# Revit family: CA_DWDI_CCW_DBD
name_source: partatom
category: Mechanical Equipment
units: mm (PartAtom-declared; Revit-internal decimal feet)

## family parameters
Always vertical = Yes
Cut with Voids When Loaded = No
Part Type = Normal
Room Calculation Point = No
Round Connector Dimension = Use Radius
Shared = No
Work Plane-Based = No

## types (60) — shared parameters
0 = 0' - 0"
1" = 0' - 1"
1.5 = 0' - 1 1/2"
2" = 0' - 2"
2' = 2' - 0"
3" = 0' - 3"
4" = 0' - 4"
Manufacturer = Loren Cook Company
Model = CA DWDI
ONE EIGTH = 0' - 0 1/8"
URL = www.lorencook.com

## per-type parameters (varying)
- 120_CA-DWDI_CCW_DBD_CLASS_1: ((B+.25")/2)=0' - 8 31/32"; (D-A-.25)/2=0' - 1 9/16"; (G/5*3)+2"=0' - 9 1/16"; (M-(B+.25"))/2=0' - 1 7/8"; -((B+.25")/2)=-0' - 8 31/32"; -B/2=-0' - 8 27/32"; -P=-2' - 4 11/16"; A=1' - 0 1/8"; A+.25"=1' - 0 3/8"; A+.25"+DB_H=1' - 2 3/8"; A/2=0' - 6 1/16"; B=1' - 5 11/16"; B+.25"=1' - 5 15/16"; B/2=0' - 8 27/32"; D=1' - 3 1/2"; D/2=0' - 7 3/4"; DB_D=2' - 0 3/8"; DB_E=1' - 1"; DB_F=2' - 1 3/4"; DB_G=1' - 3 1/16"; DB_H=0' - 2"; E=1' - 9 1/16"; E/2=0' - 10 17/32"; F=1' - 11 3/8"; F-((D-A)/2)=1' - 9 11/16"; F-.125"=1' - 11 1/4"; G=1' - 1"; G+((G/5*3)+2")=1' - 10 1/16"; G-(G/5*3)=0' - 4 15/16"; G-2.5"=0' - 11 9/16"; G/10*3=0' - 4 1/32"; G/5*3=0' - 8 1/16"; H=2' - 1 3/4"; INLET=1' - 4 1/8"; INLET/2=0' - 8 1/16"; J=0' - 10 11/16"; K=0' - 2"; L=0' - 10 27/32"; M=1' - 9 11/16"; M/2=0' - 10 27/32"; N=0' - 5 3/4"; P=2' - 4 11/16"; P-N=-1' - 10 15/16"; P-N-M=0' - 1 1/4"; R=0' - 1 7/16"; R+R=0' - 2 7/8"; R/2=0' - 0 23/32"; S=1' - 7 15/16"; T=0' - 9 31/32"; Type Comments=Airfoil Centrifugal Blower Counter-Clockwise Down Blast Arrangement 3 Class 1; U=0' - 7 1/2"; V=1' - 6"; W=0' - 0 11/16"; W/2=0' - 0 11/32"; X=1' - 9 15/16"; X/2=0' - 10 31/32"
- 135_CA-DWDI_CCW_DBD_CLASS_1: ((B+.25")/2)=0' - 10 3/32"; (D-A-.25)/2=0' - 1 9/16"; (G/5*3)+2"=0' - 9 13/16"; (M-(B+.25"))/2=0' - 1 7/8"; -((B+.25")/2)=-0' - 10 3/32"; -B/2=-0' - 9 31/32"; -P=-2' - 6 15/16"; A=1' - 1 5/8"; A+.25"=1' - 1 7/8"; A+.25"+DB_H=1' - 3 7/8"; A/2=0' - 6 13/16"; B=1' - 7 15/16"; B+.25"=1' - 8 3/16"; B/2=0' - 9 31/32"; D=1' - 5"; D/2=0' - 8 1/2"; DB_D=2' - 1 9/16"; DB_E=1' - 2"; DB_F=2' - 4 3/4"; DB_G=1' - 4 11/16"; DB_H=0' - 2"; E=1' - 11 5/16"; E/2=0' - 11 21/32"; F=2' - 1 5/8"; F-((D-A)/2)=1' - 11 15/16"; F-.125"=2' - 1 1/2"; G=1' - 2"; G+((G/5*3)+2")=1' - 11 13/16"; G-(G/5*3)=0' - 5 3/16"; G-2.5"=1' - 0 9/16"; G/10*3=0' - 4 13/32"; G/5*3=0' - 8 13/16"; H=2' - 4 3/4"; INLET=1' - 5 5/8"; INLET/2=0' - 8 13/16"; J=1' - 0 1/16"; K=0' - 2"; L=0' - 11 31/32"; M=1' - 11 15/16"; M/2=0' - 11 31/32"; N=0' - 5 3/4"; P=2' - 6 15/16"; P-N=-2' - 1 3/16"; P-N-M=0' - 1 1/4"; R=0' - 1 7/16"; R+R=0' - 2 7/8"; R/2=0' - 0 23/32"; S=1' - 10 3/16"; T=0' - 11 3/32"; Type Comments=Airfoil Centrifugal Blower Counter-Clockwise Down Blast Arrangement 3 Class 1; U=0' - 8 1/2"; V=1' - 6"; W=0' - 0 11/16"; W/2=0' - 0 11/32"; X=2' - 0 3/16"; X/2=1' - 0 3/32"
- 150_CA-DWDI_CCW_DBD_CLASS_1: ((B+.25")/2)=0' - 11 1/8"; (D-A-.25)/2=0' - 1 9/16"; (G/5*3)+2"=0' - 10 9/16"; (M-(B+.25"))/2=0' - 1 7/8"; -((B+.25")/2)=-0' - 11 1/8"; -B/2=-0' - 11"; -P=-2' - 10 1/4"; A=1' - 3 1/4"; A+.25"=1' - 3 1/2"; A+.25"+DB_H=1' - 5 1/2"; A/2=0' - 7 5/8"; B=1' - 10"; B+.25"=1' - 10 1/4"; B/2=0' - 11"; D=1' - 6 5/8"; D/2=0' - 9 5/16"; DB_D=2' - 5 1/4"; DB_E=1' - 3"; DB_F=2' - 7 5/8"; DB_G=1' - 6 5/16"; DB_H=0' - 2"; E=2' - 1 3/8"; E/2=1' - 0 11/16"; F=2' - 3 15/16"; F-((D-A)/2)=2' - 2 1/4"; F-.125"=2' - 3 13/16"; G=1' - 3"; G+((G/5*3)+2")=2' - 1 9/16"; G-(G/5*3)=0' - 5 7/16"; G-2.5"=1' - 1 5/16"; G/10*3=0' - 4 25/32"; G/5*3=0' - 9 9/16"; H=2' - 7 5/8"; INLET=1' - 7 1/8"; INLET/2=0' - 9 9/16"; J=1' - 1 5/16"; K=0' - 2"; L=1' - 1"; M=2' - 2"; M/2=1' - 1"; N=0' - 6 5/8"; P=2' - 10 1/4"; P-N=-2' - 3 5/8"; P-N-M=0' - 1 5/8"; R=0' - 1 11/16"; R+R=0' - 3 3/8"; R/2=0' - 0 27/32"; S=2' - 0 1/4"; T=1' - 0 1/8"; Type Comments=Airfoil Centrifugal Blower Counter-Clockwise Down Blast Arrangement 3 Class 1; U=0' - 9"; V=1' - 6"; W=0' - 0 11/16"; W/2=0' - 0 11/32"; X=2' - 2 1/4"; X/2=1' - 1 1/8"
- 165_CA-DWDI_CCW_DBD_CLASS_1: ((B+.25")/2)=1' - 0 1/8"; (D-A-.25)/2=0' - 1 9/16"; (G/5*3)+2"=0' - 11 19/32"; (M-(B+.25"))/2=0' - 1 7/8"; -((B+.25")/2)=-1' - 0 1/8"; -B/2=-1' - 0"; -P=-3' - 0 1/4"; A=1' - 4 15/16"; A+.25"=1' - 5 3/16"; A+.25"+DB_H=1' - 7 3/16"; A/2=0' - 8 15/32"; B=2' - 0"; B+.25"=2' - 0 1/4"; B/2=1' - 0"; D=1' - 8 5/16"; D/2=0' - 10 5/32"; DB_D=2' - 8 5/8"; DB_E=1' - 5"; DB_F=2' - 10 3/8"; DB_G=1' - 7 15/16"; DB_H=0' - 2"; E=2' - 3 3/8"; E/2=1' - 1 11/16"; F=2' - 7 1/4"; F-((D-A)/2)=2' - 5 9/16"; F-.125"=2' - 7 1/8"; G=1' - 5"; G+((G/5*3)+2")=2' - 4 19/32"; G-(G/5*3)=0' - 6 13/32"; G-2.5"=1' - 3 5/16"; G/10*3=0' - 5 5/16"; G/5*3=0' - 10 19/32"; H=2' - 10 3/8"; INLET=1' - 9 3/16"; INLET/2=0' - 10 19/32"; J=1' - 2 7/16"; K=0' - 2"; L=1' - 2"; M=2' - 4"; M/2=1' - 2"; N=0' - 6 5/8"; P=3' - 0 1/4"; P-N=-2' - 5 5/8"; P-N-M=0' - 1 5/8"; R=0' - 1 11/16"; R+R=0' - 3 3/8"; R/2=0' - 0 27/32"; S=2' - 2 1/4"; T=1' - 1 1/8"; Type Comments=Airfoil Centrifugal Blower Counter-Clockwise Down Blast Arrangement 3 Class 1; U=0' - 10"; V=1' - 6"; W=0' - 0 11/16"; W/2=0' - 0 11/32"; X=2' - 4 1/4"; X/2=1' - 2 1/8"
- 180_CA-DWDI_CCW_DBD_CLASS_1: ((B+.25")/2)=1' - 1 5/32"; (D-A-.25)/2=0' - 1 9/16"; (G/5*3)+2"=1' - 0 11/32"; (M-(B+.25"))/2=0' - 1 7/8"; -((B+.25")/2)=-1' - 1 5/32"; -B/2=-1' - 1 1/32"; -P=-3' - 2 13/16"; A=1' - 6 1/2"; A+.25"=1' - 6 3/4"; A+.25"+DB_H=1' - 8 3/4"; A/2=0' - 9 1/4"; B=2' - 2 1/16"; B+.25"=2' - 2 5/16"; B/2=1' - 1 1/32"; D=1' - 9 7/8"; D/2=0' - 10 15/16"; DB_D=2' - 11 1/8"; DB_E=1' - 6"; DB_F=3' - 1 1/8"; DB_G=1' - 9 9/16"; DB_H=0' - 2"; E=2' - 5 7/16"; E/2=1' - 2 23/32"; F=2' - 9 1/2"; F-((D-A)/2)=2' - 7 13/16"; F-.125"=2' - 9 3/8"; G=1' - 6"; G+((G/5*3)+2")=2' - 6 11/32"; G-(G/5*3)=0' - 6 21/32"; G-2.5"=1' - 4 5/16"; G/10*3=0' - 5 11/16"; G/5*3=0' - 11 11/32"; H=3' - 1 1/8"; INLET=1' - 10 11/16"; INLET/2=0' - 11 11/32"; J=1' - 3 9/16"; K=0' - 2"; L=1' - 3 1/32"; M=2' - 6 1/16"; M/2=1' - 3 1/32"; N=0' - 7 1/8"; P=3' - 2 13/16"; P-N=-2' - 7 11/16"; P-N-M=0' - 1 5/8"; R=0' - 1 11/16"; R+R=0' - 3 3/8"; R/2=0' - 0 27/32"; S=2' - 4 5/16"; T=1' - 2 5/32"; Type Comments=Airfoil Centrifugal Blower Counter-Clockwise Down Blast Arrangement 3 Class 1; U=0' - 11"; V=1' - 6"; W=0' - 0 11/16"; W/2=0' - 0 11/32"; X=2' - 6 5/16"; X/2=1' - 3 5/32"
- 195_CA-DWDI_CCW_DBD_CLASS_1: ((B+.25")/2)=1' - 2 11/32"; (D-A-.25)/2=0' - 1 9/16"; (G/5*3)+2"=1' - 1 3/32"; (M-(B+.25"))/2=0' - 1 7/8"; -((B+.25")/2)=-1' - 2 11/32"; -B/2=-1' - 2 7/32"; -P=-3' - 5 11/16"; A=1' - 7 1/2"; A+.25"=1' - 7 3/4"; A+.25"+DB_H=1' - 9 3/4"; A/2=0' - 9 3/4"; B=2' - 4 7/16"; B+.25"=2' - 4 11/16"; B/2=1' - 2 7/32"; D=1' - 10 7/8"; D/2=0' - 11 7/16"; DB_D=3' - 2 1/2"; DB_E=1' - 8"; DB_F=3' - 4"; DB_G=1' - 11 3/16"; DB_H=0' - 2"; E=2' - 7 13/16"; E/2=1' - 3 29/32"; F=3' - 0 13/16"; F-((D-A)/2)=2' - 11 1/8"; F-.125"=3' - 0 11/16"; G=1' - 8"; G+((G/5*3)+2")=2' - 9 3/32"; G-(G/5*3)=0' - 7 29/32"; G-2.5"=1' - 6 1/16"; G/10*3=0' - 6 1/16"; G/5*3=1' - 0 3/32"; H=3' - 4"; INLET=2' - 0 3/16"; INLET/2=1' - 0 3/32"; J=1' - 4 13/16"; K=0' - 2"; L=1' - 4 7/32"; M=2' - 8 7/16"; M/2=1' - 4 7/32"; N=0' - 7 1/4"; P=3' - 5 11/16"; P-N=-2' - 10 7/16"; P-N-M=0' - 2"; R=0' - 1 15/16"; R+R=0' - 3 7/8"; R/2=0' - 0 31/32"; S=2' - 6 11/16"; T=1' - 3 11/32"; Type Comments=Airfoil Centrifugal Blower Counter-Clockwise Down Blast Arrangement 3 Class 1; U=0' - 11 1/2"; V=0' - 6"; W=0' - 0 11/16"; W/2=0' - 0 11/32"; X=2' - 8 11/16"; X/2=1' - 4 11/32"
- 210_CA-DWDI_CCW_DBD_CLASS_1: ((B+.25")/2)=1' - 3 5/16"; (D-A-.25)/2=0' - 1 9/16"; (G/5*3)+2"=1' - 1 31/32"; (M-(B+.25"))/2=0' - 1 7/8"; -((B+.25")/2)=-1' - 3 5/16"; -B/2=-1' - 3 3/16"; -P=-3' - 8 1/8"; A=1' - 9 5/8"; A+.25"=1' - 9 7/8"; A+.25"+DB_H=1' - 11 7/8"; A/2=0' - 10 13/16"; B=2' - 6 3/8"; B+.25"=2' - 6 5/8"; B/2=1' - 3 3/16"; D=2' - 1"; D/2=1' - 0 1/2"; DB_D=3' - 4 15/16"; DB_E=1' - 9"; DB_F=3' - 6 7/8"; DB_G=2' - 0 7/8"; DB_H=0' - 2"; E=2' - 9 3/4"; E/2=1' - 4 7/8"; F=3' - 3 1/8"; F-((D-A)/2)=3' - 1 7/16"; F-.125"=3' - 3"; G=1' - 9"; G+((G/5*3)+2")=2' - 10 31/32"; G-(G/5*3)=0' - 8 1/32"; G-2.5"=1' - 7 1/16"; G/10*3=0' - 6 1/2"; G/5*3=1' - 0 31/32"; H=3' - 6 7/8"; INLET=2' - 1 15/16"; INLET/2=1' - 0 31/32"; J=1' - 6"; K=0' - 2"; L=1' - 5 3/16"; M=2' - 10 3/8"; M/2=1' - 5 3/16"; N=0' - 7 7/8"; P=3' - 8 1/8"; P-N=-3' - 0 1/4"; P-N-M=0' - 1 7/8"; R=0' - 1 15/16"; R+R=0' - 3 7/8"; R/2=0' - 0 31/32"; S=2' - 8 5/8"; T=1' - 4 5/16"; Type Comments=Airfoil Centrifugal Blower Counter-Clockwise Down Blast Arrangement 3 Class 1; U=1' - 0"; V=0' - 7"; W=0' - 0 13/16"; W/2=0' - 0 13/32"; X=2' - 10 5/8"; X/2=1' - 5 5/16"
- 225_CA-DWDI_CCW_DBD_CLASS_1: ((B+.25")/2)=1' - 4 3/8"; (D-A-.25)/2=0' - 1 9/16"; (G/5*3)+2"=1' - 2 23/32"; (M-(B+.25"))/2=0' - 1 7/8"; -((B+.25")/2)=-1' - 4 3/8"; -B/2=-1' - 4 1/4"; -P=-4' - 0 1/4"; A=1' - 11 3/16"; A+.25"=1' - 11 7/16"; A+.25"+DB_H=2' - 1 7/16"; A/2=0' - 11 19/32"; B=2' - 8 1/2"; B+.25"=2' - 8 3/4"; B/2=1' - 4 1/4"; D=2' - 2 9/16"; D/2=1' - 1 9/32"; DB_D=3' - 8 3/8"; DB_E=1' - 11"; DB_F=3' - 9 3/4"; DB_G=2' - 2 1/2"; DB_H=0' - 2"; E=2' - 11 7/8"; E/2=1' - 5 15/16"; F=3' - 6 3/8"; F-((D-A)/2)=3' - 4 11/16"; F-.125"=3' - 6 1/4"; G=1' - 11"; G+((G/5*3)+2")=3' - 1 23/32"; G-(G/5*3)=0' - 9 9/32"; G-2.5"=1' - 9 1/16"; G/10*3=0' - 6 7/8"; G/5*3=1' - 1 23/32"; H=3' - 9 3/4"; INLET=2' - 3 7/16"; INLET/2=1' - 1 23/32"; J=1' - 7 1/4"; K=0' - 2"; L=1' - 6 1/4"; M=3' - 0 1/2"; M/2=1' - 6 1/4"; N=0' - 7 7/8"; P=4' - 0 1/4"; P-N=-3' - 4 3/8"; P-N-M=0' - 3 7/8"; R=0' - 1 15/16"; R+R=0' - 3 7/8"; R/2=0' - 0 31/32"; S=2' - 10 3/4"; T=1' - 5 3/8"; Type Comments=Airfoil Centrifugal Blower Counter-Clockwise Down Blast Arrangement 3 Class 1; U=1' - 0 1/2"; V=0' - 7 1/2"; W=0' - 0 13/16"; W/2=0' - 0 13/32"; X=3' - 0 3/4"; X/2=1' - 6 3/8"
- 245_CA-DWDI_CCW_DBD_CLASS_1: ((B+.25")/2)=1' - 5 21/32"; (D-A-.25)/2=0' - 1 9/16"; (G/5*3)+2"=1' - 3 23/32"; (M-(B+.25"))/2=0' - 1 7/8"; -((B+.25")/2)=-1' - 5 21/32"; -B/2=-1' - 5 17/32"; -P=-4' - 1 13/16"; A=2' - 1 1/2"; A+.25"=2' - 1 3/4"; A+.25"+DB_H=2' - 3 3/4"; A/2=1' - 0 3/4"; B=2' - 11 1/16"; B+.25"=2' - 11 5/16"; B/2=1' - 5 17/32"; D=2' - 4 7/8"; D/2=1' - 2 7/16"; DB_D=4' - 0 1/4"; DB_E=2' - 1"; DB_F=4' - 1 1/2"; DB_G=2' - 4 5/8"; DB_H=0' - 2"; E=3' - 2 7/16"; E/2=1' - 7 7/32"; F=3' - 10 1/8"; F-((D-A)/2)=3' - 8 7/16"; F-.125"=3' - 10"; G=2' - 1"; G+((G/5*3)+2")=3' - 4 23/32"; G-(G/5*3)=0' - 10 9/32"; G-2.5"=1' - 10 13/16"; G/10*3=0' - 7 3/8"; G/5*3=1' - 2 23/32"; H=4' - 1 1/2"; INLET=2' - 5 7/16"; INLET/2=1' - 2 23/32"; J=1' - 8 7/8"; K=0' - 2"; L=1' - 7 17/32"; M=3' - 3 1/16"; M/2=1' - 7 17/32"; N=0' - 8 5/8"; P=4' - 1 13/16"; P-N=-3' - 5 3/16"; P-N-M=0' - 2 1/8"; R=0' - 2 3/16"; R+R=0' - 4 3/8"; R/2=0' - 1 3/32"; S=3' - 1 5/16"; T=1' - 6 21/32"; Type Comments=Airfoil Centrifugal Blower Counter-Clockwise Down Blast Arrangement 3 Class 1; U=1' - 1 1/2"; V=0' - 8"; W=0' - 0 13/16"; W/2=0' - 0 13/32"; X=3' - 5 5/16"; X/2=1' - 8 21/32"
- 270_CA-DWDI_CCW_DBD_CLASS_1: ((B+.25")/2)=1' - 7 27/32"; (D-A-.25)/2=0' - 1 9/16"; (G/5*3)+2"=1' - 4 31/32"; (M-(B+.25"))/2=0' - 1 7/8"; -((B+.25")/2)=-1' - 7 27/32"; -B/2=-1' - 7 23/32"; -P=-4' - 6 3/16"; A=2' - 3 1/2"; A+.25"=2' - 3 3/4"; A+.25"+DB_H=2' - 5 3/4"; A/2=1' - 1 3/4"; B=3' - 3 7/16"; B+.25"=3' - 3 11/16"; B/2=1' - 7 23/32"; D=2' - 6 7/8"; D/2=1' - 3 7/16"; DB_D=4' - 2 1/8"; DB_E=2' - 3"; DB_F=4' - 6 3/4"; DB_G=2' - 7 3/8"; DB_H=0' - 2"; E=3' - 6 13/16"; E/2=1' - 9 13/32"; F=4' - 2 1/4"; F-((D-A)/2)=4' - 0 9/16"; F-.125"=4' - 2 1/8"; G=2' - 3"; G+((G/5*3)+2")=3' - 7 31/32"; G-(G/5*3)=0' - 11 1/32"; G-2.5"=2' - 0 13/16"; G/10*3=0' - 8"; G/5*3=1' - 3 31/32"; H=4' - 6 3/4"; INLET=2' - 7 15/16"; INLET/2=1' - 3 31/32"; J=1' - 11 3/8"; K=0' - 2"; L=1' - 9 23/32"; M=3' - 7 7/16"; M/2=1' - 9 23/32"; N=0' - 8 5/8"; P=4' - 6 3/16"; P-N=-3' - 9 9/16"; P-N-M=0' - 2 1/8"; R=0' - 2 3/16"; R+R=0' - 4 3/8"; R/2=0' - 1 3/32"; S=3' - 5 11/16"; T=1' - 8 27/32"; Type Comments=Airfoil Centrifugal Blower Counter-Clockwise Down Blast Arrangement 3 Class 1; U=1' - 3"; V=0' - 9"; W=0' - 0 13/16"; W/2=0' - 0 13/32"; X=3' - 9 11/16"; X/2=1' - 10 27/32"
- 300_CA-DWDI_CCW_DBD_CLASS_1: ((B+.25")/2)=1' - 9 5/8"; (D-A-.25)/2=0' - 1 19/32"; (G/5*3)+2"=1' - 6 15/32"; (M-(B+.25"))/2=0' - 1 7/8"; -((B+.25")/2)=-1' - 9 5/8"; -B/2=-1' - 9 1/2"; -P=-4' - 10 1/2"; A=2' - 7 3/16"; A+.25"=2' - 7 7/16"; A+.25"+DB_H=2' - 9 7/16"; A/2=1' - 3 19/32"; B=3' - 7"; B+.25"=3' - 7 1/4"; B/2=1' - 9 1/2"; D=2' - 10 5/8"; D/2=1' - 5 5/16"; DB_D=4' - 10 1/2"; DB_E=2' - 6"; DB_F=5' - 0"; DB_G=2' - 10 5/8"; DB_H=0' - 2"; E=3' - 10 7/16"; E/2=1' - 11 7/32"; F=4' - 7 7/8"; F-((D-A)/2)=4' - 6 5/32"; F-.125"=4' - 7 3/4"; G=2' - 6"; G+((G/5*3)+2")=4' - 0 15/32"; G-(G/5*3)=1' - 0 17/32"; G-2.5"=2' - 3 9/16"; G/10*3=0' - 8 3/4"; G/5*3=1' - 5 15/32"; H=5' - 0"; INLET=2' - 10 15/16"; INLET/2=1' - 5 15/32"; J=2' - 1 3/8"; K=0' - 2"; L=1' - 11 1/2"; M=3' - 11"; M/2=1' - 11 1/2"; N=0' - 9 1/4"; P=4' - 10 1/2"; P-N=-4' - 1 1/4"; P-N-M=0' - 2 1/4"; R=0' - 2 7/16"; R+R=0' - 4 7/8"; R/2=0' - 1 7/32"; S=3' - 9 1/4"; T=1' - 10 5/8"; Type Comments=Airfoil Centrifugal Blower Counter-Clockwise Down Blast Arrangement 3 Class 1; U=1' - 4 1/2"; V=0' - 10"; W=0' - 0 13/16"; W/2=0' - 0 13/32"; X=4' - 1 1/4"; X/2=2' - 0 5/8"
- 330_CA-DWDI_CCW_DBD_CLASS_1: ((B+.25")/2)=1' - 11 21/32"; (D-A-.25)/2=0' - 2 3/32"; (G/5*3)+2"=1' - 7 31/32"; (M-(B+.25"))/2=0' - 1 7/8"; -((B+.25")/2)=-1' - 11 21/32"; -B/2=-1' - 11 17/32"; -P=-5' - 3 9/16"; A=2' - 10 1/2"; A+.25"=2' - 10 3/4"; A+.25"+DB_H=3' - 0 3/4"; A/2=1' - 5 1/4"; B=3' - 11 1/16"; B+.25"=3' - 11 5/16"; B/2=1' - 11 17/32"; D=3' - 2 15/16"; D/2=1' - 7 15/32"; DB_D=5' - 4 3/8"; DB_E=2' - 9"; DB_F=5' - 5 3/4"; DB_G=3' - 1 7/8"; DB_H=0' - 2"; E=4' - 3 1/2"; E/2=2' - 1 3/4"; F=5' - 1 3/8"; F-((D-A)/2)=4' - 11 5/32"; F-.125"=5' - 1 1/4"; G=2' - 9"; G+((G/5*3)+2")=4' - 4 31/32"; G-(G/5*3)=1' - 2 1/32"; G-2.5"=2' - 6 5/16"; G/10*3=0' - 9 1/2"; G/5*3=1' - 6 31/32"; H=5' - 5 3/4"; INLET=3' - 1 15/16"; INLET/2=1' - 6 31/32"; J=2' - 3 7/8"; K=0' - 2"; L=2' - 1 17/32"; M=4' - 3 1/16"; M/2=2' - 1 17/32"; N=0' - 10 1/16"; P=5' - 3 9/16"; P-N=-4' - 5 1/2"; P-N-M=0' - 2 7/16"; R=0' - 2 11/16"; R+R=0' - 5 3/8"; R/2=0' - 1 11/32"; S=4' - 1 5/16"; T=2' - 0 21/32"; Type Comments=Airfoil Centrifugal Blower Counter-Clockwise Down Blast Arrangement 3 Class 1; U=1' - 6"; V=1' - 0"; W=0' - 0 13/16"; W/2=0' - 0 13/32"; X=4' - 5 7/16"; X/2=2' - 2 23/32"
- 365_CA-DWDI_CCW_DBD_CLASS_1: ((B+.25")/2)=2' - 2 7/32"; (D-A-.25)/2=0' - 2 3/32"; (G/5*3)+2"=1' - 9 23/32"; (M-(B+.25"))/2=0' - 1 7/8"; -((B+.25")/2)=-2' - 2 7/32"; -B/2=-2' - 2 3/32"; -P=-5' - 9 5/16"; A=3' - 2 11/16"; A+.25"=3' - 2 15/16"; A+.25"+DB_H=3' - 4 15/16"; A/2=1' - 7 11/32"; B=4' - 4 3/16"; B+.25"=4' - 4 7/16"; B/2=2' - 2 3/32"; D=3' - 7 1/8"; D/2=1' - 9 9/16"; DB_D=5' - 10 5/8"; DB_E=3' - 0"; DB_F=6' - 0 3/8"; DB_G=3' - 5 3/4"; DB_H=0' - 2"; E=4' - 8 5/8"; E/2=2' - 4 5/16"; F=5' - 7 7/16"; F-((D-A)/2)=5' - 5 7/32"; F-.125"=5' - 7 5/16"; G=3' - 0"; G+((G/5*3)+2")=4' - 9 23/32"; G-(G/5*3)=1' - 3 9/32"; G-2.5"=2' - 9 13/16"; G/10*3=0' - 10 3/8"; G/5*3=1' - 8 23/32"; H=6' - 0 3/8"; INLET=3' - 5 7/16"; INLET/2=1' - 8 23/32"; J=2' - 6 5/8"; K=0' - 2"; L=2' - 4 3/32"; M=4' - 8 3/16"; M/2=2' - 4 3/32"; N=0' - 10 5/16"; P=5' - 9 5/16"; P-N=-4' - 11"; P-N-M=0' - 2 13/16"; R=0' - 2 3/16"; R+R=0' - 4 3/8"; R/2=0' - 1 3/32"; S=4' - 6 7/16"; T=2' - 3 7/32"; Type Comments=Airfoil Centrifugal Blower Counter-Clockwise Down Blast Arrangement 3 Class 1; U=1' - 8"; V=1' - 1"; W=0' - 0 13/16"; W/2=0' - 0 13/32"; X=4' - 10 9/16"; X/2=2' - 5 9/32"
- 402_CA-DWDI_CCW_DBD_CLASS_1: ((B+.25")/2)=2' - 5 1/32"; (D-A-.25)/2=0' - 2 3/32"; (G/5*3)+2"=1' - 11 19/32"; (M-(B+.25"))/2=0' - 2 7/8"; -((B+.25")/2)=-2' - 5 1/32"; -B/2=-2' - 4 29/32"; -P=-6' - 3 11/16"; A=3' - 5 3/4"; A+.25"=3' - 6"; A+.25"+DB_H=3' - 9"; A/2=1' - 8 7/8"; B=4' - 9 13/16"; B+.25"=4' - 10 1/16"; B/2=2' - 4 29/32"; D=3' - 10 3/16"; D/2=1' - 11 3/32"; DB_D=6' - 6 1/4"; DB_E=3' - 4"; DB_F=6' - 8 3/8"; DB_G=3' - 10 3/4"; DB_H=0' - 3"; E=5' - 2 1/4"; E/2=2' - 7 1/8"; F=6' - 2 11/16"; F-((D-A)/2)=6' - 0 15/32"; F-.125"=6' - 2 9/16"; G=3' - 4"; G+((G/5*3)+2")=5' - 3 19/32"; G-(G/5*3)=1' - 5 13/32"; G-2.5"=3' - 1 9/16"; G/10*3=0' - 11 5/16"; G/5*3=1' - 10 19/32"; H=6' - 8 3/8"; INLET=3' - 9 3/16"; INLET/2=1' - 10 19/32"; J=2' - 9 5/8"; K=0' - 3"; L=2' - 7 29/32"; M=5' - 3 13/16"; M/2=2' - 7 29/32"; N=0' - 10"; P=6' - 3 11/16"; P-N=-5' - 5 11/16"; P-N-M=0' - 1 7/8"; R=0' - 2 7/16"; R+R=0' - 4 7/8"; R/2=0' - 1 7/32"; S=5' - 1 5/16"; T=2' - 6 21/32"; Type Comments=Airfoil Centrifugal Blower Counter-Clockwise Down Blast Arrangement 3 Class 1; U=1' - 10"; V=1' - 2"; W=0' - 1 1/16"; W/2=0' - 0 17/32"; X=5' - 5 3/16"; X/2=2' - 8 19/32"
- 445_CA-DWDI_CCW_DBD_CLASS_1: ((B+.25")/2)=2' - 8 1/4"; (D-A-.25)/2=0' - 2 3/32"; (G/5*3)+2"=2' - 1 23/32"; (M-(B+.25"))/2=0' - 2 7/8"; -((B+.25")/2)=-2' - 8 1/4"; -B/2=-2' - 8 1/8"; -P=-6' - 10 5/8"; A=3' - 9 15/16"; A+.25"=3' - 10 3/16"; A+.25"+DB_H=4' - 1 3/16"; A/2=1' - 10 31/32"; B=5' - 4 1/4"; B+.25"=5' - 4 1/2"; B/2=2' - 8 1/8"; D=4' - 2 3/8"; D/2=2' - 1 3/16"; DB_D=7' - 2 1/4"; DB_E=3' - 8"; DB_F=7' - 4 1/2"; DB_G=4' - 3 3/8"; DB_H=0' - 3"; E=5' - 8 11/16"; E/2=2' - 10 11/32"; F=6' - 10 5/16"; F-((D-A)/2)=6' - 8 3/32"; F-.125"=6' - 10 3/16"; G=3' - 8"; G+((G/5*3)+2")=5' - 9 23/32"; G-(G/5*3)=1' - 7 9/32"; G-2.5"=3' - 5 9/16"; G/10*3=1' - 0 3/8"; G/5*3=2' - 0 23/32"; H=7' - 4 1/2"; INLET=4' - 1 7/16"; INLET/2=2' - 0 23/32"; J=3' - 1 1/8"; K=0' - 3"; L=2' - 11 1/8"; M=5' - 10 1/4"; M/2=2' - 11 1/8"; N=0' - 10 5/8"; P=6' - 10 5/8"; P-N=-6' - 0"; P-N-M=0' - 1 3/4"; R=0' - 2 7/16"; R+R=0' - 4 7/8"; R/2=0' - 1 7/32"; S=5' - 7 3/4"; T=2' - 9 7/8"; Type Comments=Airfoil Centrifugal Blower Counter-Clockwise Down Blast Arrangement 3 Class 1; U=2' - 0"; V=1' - 4"; W=0' - 1 1/16"; W/2=0' - 0 17/32"; X=5' - 11 5/8"; X/2=2' - 11 13/16"
- 490_CA-DWDI_CCW_DBD_CLASS_1: ((B+.25")/2)=2' - 11 3/16"; (D-A-.25)/2=0' - 2 3/32"; (G/5*3)+2"=2' - 4 1/2"; (M-(B+.25"))/2=0' - 2 7/8"; -((B+.25")/2)=-2' - 11 3/16"; -B/2=-2' - 11 1/16"; -P=-7' - 5 1/2"; A=4' - 3"; A+.25"=4' - 3 1/4"; A+.25"+DB_H=4' - 6 1/4"; A/2=2' - 1 1/2"; B=5' - 10 1/8"; B+.25"=5' - 10 3/8"; B/2=2' - 11 1/16"; D=4' - 7 7/16"; D/2=2' - 3 23/32"; DB_D=7' - 10 1/2"; DB_E=4' - 0"; DB_F=8' - 1"; DB_G=4' - 8 1/4"; DB_H=0' - 3"; E=6' - 2 9/16"; E/2=3' - 1 9/32"; F=7' - 6 3/16"; F-((D-A)/2)=7' - 3 31/32"; F-.125"=7' - 6 1/16"; G=4' - 0"; G+((G/5*3)+2")=6' - 4 1/2"; G-(G/5*3)=1' - 8 1/2"; G-2.5"=3' - 9 1/16"; G/10*3=1' - 1 3/4"; G/5*3=2' - 3 1/2"; H=8' - 1"; INLET=4' - 7"; INLET/2=2' - 3 1/2"; J=3' - 4 3/4"; K=0' - 3"; L=3' - 2 1/16"; M=6' - 4 1/8"; M/2=3' - 2 1/16"; N=0' - 11 1/2"; P=7' - 5 1/2"; P-N=-6' - 6"; P-N-M=0' - 1 7/8"; R=0' - 2 15/16"; R+R=0' - 5 7/8"; R/2=0' - 1 15/32"; S=6' - 1 5/8"; T=3' - 0 13/16"; Type Comments=Airfoil Centrifugal Blower Counter-Clockwise Down Blast Arrangement 3 Class 1; U=2' - 2 1/2"; V=1' - 6"; W=0' - 1 1/16"; W/2=0' - 0 17/32"; X=6' - 5 1/2"; X/2=3' - 2 3/4"
- 540_CA-DWDI_CCW_DBD_CLASS_1: ((B+.25")/2)=3' - 3 3/32"; (D-A-.25)/2=0' - 2 3/32"; (G/5*3)+2"=2' - 7"; (M-(B+.25"))/2=0' - 2 7/8"; -((B+.25")/2)=-3' - 3 3/32"; -B/2=-3' - 2 31/32"; -P=-8' - 2 5/16"; A=4' - 7 3/4"; A+.25"=4' - 8"; A+.25"+DB_H=4' - 11"; A/2=2' - 3 7/8"; B=6' - 5 15/16"; B+.25"=6' - 6 3/16"; B/2=3' - 2 31/32"; D=5' - 0 3/16"; D/2=2' - 6 3/32"; DB_D=8' - 8 1/4"; DB_E=4' - 5"; DB_F=8' - 10 5/8"; DB_G=5' - 1 3/4"; DB_H=0' - 3"; E=6' - 10 3/8"; E/2=3' - 5 3/16"; F=8' - 3 1/2"; F-((D-A)/2)=8' - 1 9/32"; F-.125"=8' - 3 3/8"; G=4' - 5"; G+((G/5*3)+2")=7' - 0"; G-(G/5*3)=1' - 11"; G-2.5"=4' - 1 9/16"; G/10*3=1' - 3"; G/5*3=2' - 6"; H=8' - 10 5/8"; INLET=5' - 0"; INLET/2=2' - 6"; J=3' - 8 7/8"; K=0' - 3"; L=3' - 5 31/32"; M=6' - 11 15/16"; M/2=3' - 5 31/32"; N=1' - 0 7/16"; P=8' - 2 5/16"; P-N=-7' - 1 7/8"; P-N-M=0' - 1 15/16"; R=0' - 3 7/16"; R+R=0' - 6 7/8"; R/2=0' - 1 23/32"; S=6' - 9 7/16"; T=3' - 4 23/32"; Type Comments=Airfoil Centrifugal Blower Counter-Clockwise Down Blast Arrangement 3 Class 1; U=2' - 5"; V=1' - 8"; W=0' - 1 1/16"; W/2=0' - 0 17/32"; X=7' - 4 5/16"; X/2=3' - 8 5/32"
- 600_CA-DWDI_CCW_DBD_CLASS_1: ((B+.25")/2)=3' - 7 1/4"; (D-A-.25)/2=0' - 2 3/32"; (G/5*3)+2"=2' - 10"; (M-(B+.25"))/2=0' - 2 7/8"; -((B+.25")/2)=-3' - 7 1/4"; -B/2=-3' - 7 1/8"; -P=-8' - 11 1/2"; A=5' - 2 3/16"; A+.25"=5' - 2 7/16"; A+.25"+DB_H=5' - 5 7/16"; A/2=2' - 7 3/32"; B=7' - 2 1/4"; B+.25"=7' - 2 1/2"; B/2=3' - 7 1/8"; D=5' - 6 5/8"; D/2=2' - 9 5/16"; DB_D=9' - 8"; DB_E=4' - 11"; DB_F=9' - 10"; DB_G=5' - 8 1/4"; DB_H=0' - 3"; E=7' - 6 11/16"; E/2=3' - 9 11/32"; F=9' - 2 11/16"; F-((D-A)/2)=9' - 0 15/32"; F-.125"=9' - 2 9/16"; G=4' - 11"; G+((G/5*3)+2")=7' - 9"; G-(G/5*3)=2' - 2"; G-2.5"=4' - 7 9/16"; G/10*3=1' - 4 1/2"; G/5*3=2' - 9"; H=9' - 10"; INLET=5' - 6"; INLET/2=2' - 9"; J=4' - 1 3/4"; K=0' - 3"; L=3' - 10 1/8"; M=7' - 8 1/4"; M/2=3' - 10 1/8"; N=1' - 1"; P=8' - 11 1/2"; P-N=-7' - 10 1/2"; P-N-M=0' - 2 1/4"; R=0' - 3 7/16"; R+R=0' - 6 7/8"; R/2=0' - 1 23/32"; S=7' - 5 3/4"; T=3' - 8 7/8"; Type Comments=Airfoil Centrifugal Blower Counter-Clockwise Down Blast Arrangement 3 Class 1; U=2' - 8"; V=1' - 10"; W=0' - 1 1/16"; W/2=0' - 0 17/32"; X=8' - 0 5/8"; X/2=4' - 0 5/16"
- 660_CA-DWDI_CCW_DBD_CLASS_1: ((B+.25")/2)=3' - 11 9/16"; (D-A-.25)/2=0' - 2 3/32"; (G/5*3)+2"=3' - 1"; (M-(B+.25"))/2=0' - 2 7/8"; -((B+.25")/2)=-3' - 11 9/16"; -B/2=-3' - 11 7/16"; -P=-9' - 9 7/8"; A=5' - 8 7/16"; A+.25"=5' - 8 11/16"; A+.25"+DB_H=5' - 11 11/16"; A/2=2' - 10 7/32"; B=7' - 10 7/8"; B+.25"=7' - 11 1/8"; B/2=3' - 11 7/16"; D=6' - 0 7/8"; D/2=3' - 0 7/16"; DB_D=10' - 1 5/8"; DB_E=5' - 5"; DB_F=10' - 9 3/8"; DB_G=6' - 2 3/4"; DB_H=0' - 3"; E=8' - 3 5/16"; E/2=4' - 1 21/32"; F=10' - 1 7/8"; F-((D-A)/2)=9' - 11 21/32"; F-.125"=10' - 1 3/4"; G=5' - 5"; G+((G/5*3)+2")=8' - 6"; G-(G/5*3)=2' - 5"; G-2.5"=5' - 1 1/16"; G/10*3=1' - 6"; G/5*3=3' - 0"; H=10' - 9 3/8"; INLET=6' - 0"; INLET/2=3' - 0"; J=4' - 6 5/8"; K=0' - 3"; L=4' - 2 7/16"; M=8' - 4 7/8"; M/2=4' - 2 7/16"; N=1' - 2 13/16"; P=9' - 9 7/8"; P-N=-8' - 7 1/16"; P-N-M=0' - 2 3/16"; R=0' - 3 15/16"; R+R=0' - 7 7/8"; R/2=0' - 1 31/32"; S=8' - 2 3/8"; T=4' - 1 3/16"; Type Comments=Airfoil Centrifugal Blower Counter-Clockwise Down Blast Arrangement 3 Class 1; U=2' - 11"; V=2' - 1"; W=0' - 1 1/16"; W/2=0' - 0 17/32"; X=8' - 9 1/4"; X/2=4' - 4 5/8"
- 730 _CA-DWDI_CCW_DBD_CLASS_1: ((B+.25")/2)=4' - 4 1/2"; (D-A-.25)/2=0' - 2 3/32"; (G/5*3)+2"=3' - 4 1/2"; (M-(B+.25"))/2=0' - 2 7/8"; -((B+.25")/2)=-4' - 4 1/2"; -B/2=-4' - 4 3/8"; -P=-10' - 9 1/4"; A=6' - 3 13/16"; A+.25"=6' - 4 1/16"; A+.25"+DB_H=6' - 7 1/16"; A/2=3' - 1 29/32"; B=8' - 8 3/4"; B+.25"=8' - 9"; B/2=4' - 4 3/8"; D=6' - 8 1/4"; D/2=3' - 4 1/8"; DB_D=11' - 9 5/16"; DB_E=6' - 0"; DB_F=11' - 10 5/8"; DB_G=6' - 10 3/8"; DB_H=0' - 3"; E=9' - 1 3/16"; E/2=4' - 6 19/32"; F=11' - 2 7/8"; F-((D-A)/2)=11' - 0 21/32"; F-.125"=11' - 2 3/4"; G=6' - 0"; G+((G/5*3)+2")=9' - 4 1/2"; G-(G/5*3)=2' - 8 1/2"; G-2.5"=5' - 7 9/16"; G/10*3=1' - 7 3/4"; G/5*3=3' - 3 1/2"; H=11' - 10 5/8"; INLET=6' - 7"; INLET/2=3' - 3 1/2"; J=5' - 0 1/4"; K=0' - 3"; L=4' - 7 3/8"; M=9' - 2 3/4"; M/2=4' - 7 3/8"; N=1' - 4 5/16"; P=10' - 9 1/4"; P-N=-9' - 4 15/16"; P-N-M=0' - 2 3/16"; R=0' - 4 7/16"; R+R=0' - 8 7/8"; R/2=0' - 2 7/32"; S=9' - 0 1/4"; T=4' - 6 1/8"; Type Comments=Airfoil Centrifugal Blower Counter-Clockwise Down Blast Arrangement 3 Class 1; U=3' - 2 1/2"; V=2' - 4"; W=0' - 1 1/16"; W/2=0' - 0 17/32"; X=9' - 7 1/8"; X/2=4' - 9 9/16"
- 120_CA-DWDI_CCW_DBD_CLASS_2: ((B+.25")/2)=0' - 8 31/32"; (D-A-.25)/2=0' - 1 9/16"; (G/5*3)+2"=0' - 9 1/16"; (M-(B+.25"))/2=0' - 1 7/8"; -((B+.25")/2)=-0' - 8 31/32"; -B/2=-0' - 8 27/32"; -P=-2' - 5 7/16"; A=1' - 0 1/8"; A+.25"=1' - 0 3/8"; A+.25"+DB_H=1' - 2 3/8"; A/2=0' - 6 1/16"; B=1' - 5 11/16"; B+.25"=1' - 5 15/16"; B/2=0' - 8 27/32"; D=1' - 3 1/2"; D/2=0' - 7 3/4"; DB_D=2' - 0 3/8"; DB_E=1' - 1"; DB_F=2' - 1 3/4"; DB_G=1' - 3 1/16"; DB_H=0' - 2"; E=1' - 9 1/16"; E/2=0' - 10 17/32"; F=1' - 11 3/8"; F-((D-A)/2)=1' - 9 11/16"; F-.125"=1' - 11 1/4"; G=1' - 1"; G+((G/5*3)+2")=1' - 10 1/16"; G-(G/5*3)=0' - 4 15/16"; G-2.5"=0' - 11 5/16"; G/10*3=0' - 4 1/32"; G/5*3=0' - 8 1/16"; H=2' - 1 3/4"; INLET=1' - 4 1/8"; INLET/2=0' - 8 1/16"; J=0' - 10 11/16"; K=0' - 2"; L=0' - 10 27/32"; M=1' - 9 11/16"; M/2=0' - 10 27/32"; N=0' - 6 1/8"; P=2' - 5 7/16"; P-N=-1' - 11 5/16"; P-N-M=0' - 1 5/8"; R=0' - 1 11/16"; R+R=0' - 3 3/8"; R/2=0' - 0 27/32"; S=1' - 7 15/16"; T=0' - 9 31/32"; Type Comments=Airfoil Centrifugal Blower Counter-Clockwise Down Blast Arrangement 3 Class 2; U=0' - 7 1/2"; V=1' - 6"; W=0' - 0 11/16"; W/2=0' - 0 11/32"; X=1' - 9 15/16"; X/2=0' - 10 31/32"
- 120_CA-DWDI_CCW_DBD_CLASS_3: ((B+.25")/2)=0' - 8 31/32"; (D-A-.25)/2=0' - 1 9/16"; (G/5*3)+2"=0' - 9 1/16"; (M-(B+.25"))/2=0' - 1 7/8"; -((B+.25")/2)=-0' - 8 31/32"; -B/2=-0' - 8 27/32"; -P=-2' - 5 15/16"; A=1' - 0 1/8"; A+.25"=1' - 0 3/8"; A+.25"+DB_H=1' - 2 3/8"; A/2=0' - 6 1/16"; B=1' - 5 11/16"; B+.25"=1' - 5 15/16"; B/2=0' - 8 27/32"; D=1' - 3 1/2"; D/2=0' - 7 3/4"; DB_D=2' - 0 3/8"; DB_E=1' - 1"; DB_F=2' - 1 3/4"; DB_G=1' - 3 1/16"; DB_H=0' - 2"; E=1' - 9 1/16"; E/2=0' - 10 17/32"; F=1' - 11 3/8"; F-((D-A)/2)=1' - 9 11/16"; F-.125"=1' - 11 1/4"; G=1' - 1"; G+((G/5*3)+2")=1' - 10 1/16"; G-(G/5*3)=0' - 4 15/16"; G-2.5"=0' - 11 1/16"; G/10*3=0' - 4 1/32"; G/5*3=0' - 8 1/16"; H=2' - 1 3/4"; INLET=1' - 4 1/8"; INLET/2=0' - 8 1/16"; J=0' - 10 11/16"; K=0' - 2"; L=0' - 10 27/32"; M=1' - 9 11/16"; M/2=0' - 10 27/32"; N=0' - 6 3/8"; P=2' - 5 15/16"; P-N=-1' - 11 9/16"; P-N-M=0' - 1 7/8"; R=0' - 1 15/16"; R+R=0' - 3 7/8"; R/2=0' - 0 31/32"; S=1' - 7 15/16"; T=0' - 9 31/32"; Type Comments=Airfoil Centrifugal Blower Counter-Clockwise Down Blast Arrangement 3 Class 3; U=0' - 7 1/2"; V=1' - 6"; W=0' - 0 11/16"; W/2=0' - 0 11/32"; X=1' - 9 15/16"; X/2=0' - 10 31/32"
- 135_CA-DWDI_CCW_DBD_CLASS_2: ((B+.25")/2)=0' - 10 3/32"; (D-A-.25)/2=0' - 1 9/16"; (G/5*3)+2"=0' - 9 13/16"; (M-(B+.25"))/2=0' - 1 7/8"; -((B+.25")/2)=-0' - 10 3/32"; -B/2=-0' - 9 31/32"; -P=-2' - 7 11/16"; A=1' - 1 5/8"; A+.25"=1' - 1 7/8"; A+.25"+DB_H=1' - 3 7/8"; A/2=0' - 6 13/16"; B=1' - 7 15/16"; B+.25"=1' - 8 3/16"; B/2=0' - 9 31/32"; D=1' - 5"; D/2=0' - 8 1/2"; DB_D=2' - 1 9/16"; DB_E=1' - 2"; DB_F=2' - 4 3/4"; DB_G=1' - 4 11/16"; DB_H=0' - 2"; E=1' - 11 5/16"; E/2=0' - 11 21/32"; F=2' - 1 5/8"; F-((D-A)/2)=1' - 11 15/16"; F-.125"=2' - 1 1/2"; G=1' - 2"; G+((G/5*3)+2")=1' - 11 13/16"; G-(G/5*3)=0' - 5 3/16"; G-2.5"=1' - 0 5/16"; G/10*3=0' - 4 13/32"; G/5*3=0' - 8 13/16"; H=2' - 4 3/4"; INLET=1' - 5 5/8"; INLET/2=0' - 8 13/16"; J=1' - 0 1/16"; K=0' - 2"; L=0' - 11 31/32"; M=1' - 11 15/16"; M/2=0' - 11 31/32"; N=0' - 6 1/8"; P=2' - 7 11/16"; P-N=-2' - 1 9/16"; P-N-M=0' - 1 5/8"; R=0' - 1 11/16"; R+R=0' - 3 3/8"; R/2=0' - 0 27/32"; S=1' - 10 3/16"; T=0' - 11 3/32"; Type Comments=Airfoil Centrifugal Blower Counter-Clockwise Down Blast Arrangement 3 Class 2; U=0' - 8 1/2"; V=1' - 6"; W=0' - 0 11/16"; W/2=0' - 0 11/32"; X=2' - 0 3/16"; X/2=1' - 0 3/32"
- 135_CA-DWDI_CCW_DBD_CLASS_3: ((B+.25")/2)=0' - 10 3/32"; (D-A-.25)/2=0' - 1 9/16"; (G/5*3)+2"=0' - 9 13/16"; (M-(B+.25"))/2=0' - 1 7/8"; -((B+.25")/2)=-0' - 10 3/32"; -B/2=-0' - 9 31/32"; -P=-2' - 8 11/16"; A=1' - 1 5/8"; A+.25"=1' - 1 7/8"; A+.25"+DB_H=1' - 3 7/8"; A/2=0' - 6 13/16"; B=1' - 7 15/16"; B+.25"=1' - 8 3/16"; B/2=0' - 9 31/32"; D=1' - 5"; D/2=0' - 8 1/2"; DB_D=2' - 1 9/16"; DB_E=1' - 2"; DB_F=2' - 4 3/4"; DB_G=1' - 4 11/16"; DB_H=0' - 2"; E=1' - 11 5/16"; E/2=0' - 11 21/32"; F=2' - 1 5/8"; F-((D-A)/2)=1' - 11 15/16"; F-.125"=2' - 1 1/2"; G=1' - 2"; G+((G/5*3)+2")=1' - 11 13/16"; G-(G/5*3)=0' - 5 3/16"; G-2.5"=0' - 11 13/16"; G/10*3=0' - 4 13/32"; G/5*3=0' - 8 13/16"; H=2' - 4 3/4"; INLET=1' - 5 5/8"; INLET/2=0' - 8 13/16"; J=1' - 0 1/16"; K=0' - 2"; L=0' - 11 31/32"; M=1' - 11 15/16"; M/2=0' - 11 31/32"; N=0' - 6 5/8"; P=2' - 8 11/16"; P-N=-2' - 2 1/16"; P-N-M=0' - 2 1/8"; R=0' - 2 3/16"; R+R=0' - 4 3/8"; R/2=0' - 1 3/32"; S=1' - 10 3/16"; T=0' - 11 3/32"; Type Comments=Airfoil Centrifugal Blower Counter-Clockwise Down Blast Arrangement 3 Class 3; U=0' - 8 1/2"; V=1' - 6"; W=0' - 0 11/16"; W/2=0' - 0 11/32"; X=2' - 0 3/16"; X/2=1' - 0 3/32"
- 150_CA-DWDI_CCW_DBD_CLASS_2: ((B+.25")/2)=0' - 11 1/8"; (D-A-.25)/2=0' - 1 9/16"; (G/5*3)+2"=0' - 10 9/16"; (M-(B+.25"))/2=0' - 1 7/8"; -((B+.25")/2)=-0' - 11 1/8"; -B/2=-0' - 11"; -P=-2' - 10 3/4"; A=1' - 3 1/4"; A+.25"=1' - 3 1/2"; A+.25"+DB_H=1' - 5 1/2"; A/2=0' - 7 5/8"; B=1' - 10"; B+.25"=1' - 10 1/4"; B/2=0' - 11"; D=1' - 6 5/8"; D/2=0' - 9 5/16"; DB_D=2' - 5 1/4"; DB_E=1' - 3"; DB_F=2' - 7 5/8"; DB_G=1' - 6 5/16"; DB_H=0' - 2"; E=2' - 1 3/8"; E/2=1' - 0 11/16"; F=2' - 3 15/16"; F-((D-A)/2)=2' - 2 1/4"; F-.125"=2' - 3 13/16"; G=1' - 3"; G+((G/5*3)+2")=2' - 1 9/16"; G-(G/5*3)=0' - 5 7/16"; G-2.5"=1' - 1 1/16"; G/10*3=0' - 4 25/32"; G/5*3=0' - 9 9/16"; H=2' - 7 5/8"; INLET=1' - 7 1/8"; INLET/2=0' - 9 9/16"; J=1' - 1 5/16"; K=0' - 2"; L=1' - 1"; M=2' - 2"; M/2=1' - 1"; N=0' - 6 7/8"; P=2' - 10 3/4"; P-N=-2' - 3 7/8"; P-N-M=0' - 1 7/8"; R=0' - 1 15/16"; R+R=0' - 3 7/8"; R/2=0' - 0 31/32"; S=2' - 0 1/4"; T=1' - 0 1/8"; Type Comments=Airfoil Centrifugal Blower Counter-Clockwise Down Blast Arrangement 3 Class 2; U=0' - 9"; V=1' - 6"; W=0' - 0 11/16"; W/2=0' - 0 11/32"; X=2' - 2 1/4"; X/2=1' - 1 1/8"
- 150_CA-DWDI_CCW_DBD_CLASS_3: ((B+.25")/2)=0' - 11 1/8"; (D-A-.25)/2=0' - 1 9/16"; (G/5*3)+2"=0' - 10 9/16"; (M-(B+.25"))/2=0' - 1 7/8"; -((B+.25")/2)=-0' - 11 1/8"; -B/2=-0' - 11"; -P=-2' - 11 1/2"; A=1' - 3 1/4"; A+.25"=1' - 3 1/2"; A+.25"+DB_H=1' - 5 1/2"; A/2=0' - 7 5/8"; B=1' - 10"; B+.25"=1' - 10 1/4"; B/2=0' - 11"; D=1' - 6 5/8"; D/2=0' - 9 5/16"; DB_D=2' - 5 1/4"; DB_E=1' - 3"; DB_F=2' - 7 5/8"; DB_G=1' - 6 5/16"; DB_H=0' - 2"; E=2' - 1 3/8"; E/2=1' - 0 11/16"; F=2' - 3 15/16"; F-((D-A)/2)=2' - 2 1/4"; F-.125"=2' - 3 13/16"; G=1' - 3"; G+((G/5*3)+2")=2' - 1 9/16"; G-(G/5*3)=0' - 5 7/16"; G-2.5"=1' - 0 9/16"; G/10*3=0' - 4 25/32"; G/5*3=0' - 9 9/16"; H=2' - 7 5/8"; INLET=1' - 7 1/8"; INLET/2=0' - 9 9/16"; J=1' - 1 5/16"; K=0' - 2"; L=1' - 1"; M=2' - 2"; M/2=1' - 1"; N=0' - 7 1/4"; P=2' - 11 1/2"; P-N=-2' - 4 1/4"; P-N-M=0' - 2 1/4"; R=0' - 2 7/16"; R+R=0' - 4 7/8"; R/2=0' - 1 7/32"; S=2' - 0 1/4"; T=1' - 0 1/8"; Type Comments=Airfoil Centrifugal Blower Counter-Clockwise Down Blast Arrangement 3 Class 3; U=0' - 9"; V=1' - 6"; W=0' - 0 11/16"; W/2=0' - 0 11/32"; X=2' - 2 1/4"; X/2=1' - 1 1/8"
- 165_CA-DWDI_CCW_DBD_CLASS_2: ((B+.25")/2)=1' - 0 1/8"; (D-A-.25)/2=0' - 1 9/16"; (G/5*3)+2"=0' - 11 19/32"; (M-(B+.25"))/2=0' - 1 7/8"; -((B+.25")/2)=-1' - 0 1/8"; -B/2=-1' - 0"; -P=-3' - 0 3/4"; A=1' - 4 15/16"; A+.25"=1' - 5 3/16"; A+.25"+DB_H=1' - 7 3/16"; A/2=0' - 8 15/32"; B=2' - 0"; B+.25"=2' - 0 1/4"; B/2=1' - 0"; D=1' - 8 5/16"; D/2=0' - 10 5/32"; DB_D=2' - 8 5/8"; DB_E=1' - 5"; DB_F=2' - 10 3/8"; DB_G=1' - 7 15/16"; DB_H=0' - 2"; E=2' - 3 3/8"; E/2=1' - 1 11/16"; F=2' - 7 1/4"; F-((D-A)/2)=2' - 5 9/16"; F-.125"=2' - 7 1/8"; G=1' - 5"; G+((G/5*3)+2")=2' - 4 19/32"; G-(G/5*3)=0' - 6 13/32"; G-2.5"=1' - 3 1/16"; G/10*3=0' - 5 5/16"; G/5*3=0' - 10 19/32"; H=2' - 10 3/8"; INLET=1' - 9 3/16"; INLET/2=0' - 10 19/32"; J=1' - 2 7/16"; K=0' - 2"; L=1' - 2"; M=2' - 4"; M/2=1' - 2"; N=0' - 6 7/8"; P=3' - 0 3/4"; P-N=-2' - 5 7/8"; P-N-M=0' - 1 7/8"; R=0' - 1 15/16"; R+R=0' - 3 7/8"; R/2=0' - 0 31/32"; S=2' - 2 1/4"; T=1' - 1 1/8"; Type Comments=Airfoil Centrifugal Blower Counter-Clockwise Down Blast Arrangement 3 Class 2; U=0' - 10"; V=1' - 6"; W=0' - 0 11/16"; W/2=0' - 0 11/32"; X=2' - 4 1/4"; X/2=1' - 2 1/8"
- 165_CA-DWDI_CCW_DBD_CLASS_3: ((B+.25")/2)=1' - 0 1/8"; (D-A-.25)/2=0' - 1 9/16"; (G/5*3)+2"=0' - 11 19/32"; (M-(B+.25"))/2=0' - 1 7/8"; -((B+.25")/2)=-1' - 0 1/8"; -B/2=-1' - 0"; -P=-3' - 1 1/2"; A=1' - 4 15/16"; A+.25"=1' - 5 3/16"; A+.25"+DB_H=1' - 7 3/16"; A/2=0' - 8 15/32"; B=2' - 0"; B+.25"=2' - 0 1/4"; B/2=1' - 0"; D=1' - 8 5/16"; D/2=0' - 10 5/32"; DB_D=2' - 8 5/8"; DB_E=1' - 5"; DB_F=2' - 10 3/8"; DB_G=1' - 7 15/16"; DB_H=0' - 2"; E=2' - 3 3/8"; E/2=1' - 1 11/16"; F=2' - 7 1/4"; F-((D-A)/2)=2' - 5 9/16"; F-.125"=2' - 7 1/8"; G=1' - 5"; G+((G/5*3)+2")=2' - 4 19/32"; G-(G/5*3)=0' - 6 13/32"; G-2.5"=1' - 2 9/16"; G/10*3=0' - 5 5/16"; G/5*3=0' - 10 19/32"; H=2' - 10 3/8"; INLET=1' - 9 3/16"; INLET/2=0' - 10 19/32"; J=1' - 2 7/16"; K=0' - 2"; L=1' - 2"; M=2' - 4"; M/2=1' - 2"; N=0' - 7 3/16"; P=3' - 1 1/2"; P-N=-2' - 6 5/16"; P-N-M=0' - 2 5/16"; R=0' - 2 7/16"; R+R=0' - 4 7/8"; R/2=0' - 1 7/32"; S=2' - 2 1/4"; T=1' - 1 1/8"; Type Comments=Airfoil Centrifugal Blower Counter-Clockwise Down Blast Arrangement 3 Class 3; U=0' - 10"; V=1' - 6"; W=0' - 0 11/16"; W/2=0' - 0 11/32"; X=2' - 4 1/4"; X/2=1' - 2 1/8"
- 180_CA-DWDI_CCW_DBD_CLASS_2: ((B+.25")/2)=1' - 1 5/32"; (D-A-.25)/2=0' - 1 9/16"; (G/5*3)+2"=1' - 0 11/32"; (M-(B+.25"))/2=0' - 1 7/8"; -((B+.25")/2)=-1' - 1 5/32"; -B/2=-1' - 1 1/32"; -P=-3' - 3 5/16"; A=1' - 6 1/2"; A+.25"=1' - 6 3/4"; A+.25"+DB_H=1' - 8 3/4"; A/2=0' - 9 1/4"; B=2' - 2 1/16"; B+.25"=2' - 2 5/16"; B/2=1' - 1 1/32"; D=1' - 9 7/8"; D/2=0' - 10 15/16"; DB_D=2' - 11 1/8"; DB_E=1' - 6"; DB_F=3' - 1 1/8"; DB_G=1' - 9 9/16"; DB_H=0' - 2"; E=2' - 5 7/16"; E/2=1' - 2 23/32"; F=2' - 9 1/2"; F-((D-A)/2)=2' - 7 13/16"; F-.125"=2' - 9 3/8"; G=1' - 6"; G+((G/5*3)+2")=2' - 6 11/32"; G-(G/5*3)=0' - 6 21/32"; G-2.5"=1' - 4 1/16"; G/10*3=0' - 5 11/16"; G/5*3=0' - 11 11/32"; H=3' - 1 1/8"; INLET=1' - 10 11/16"; INLET/2=0' - 11 11/32"; J=1' - 3 9/16"; K=0' - 2"; L=1' - 3 1/32"; M=2' - 6 1/16"; M/2=1' - 3 1/32"; N=0' - 7 3/8"; P=3' - 3 5/16"; P-N=-2' - 7 15/16"; P-N-M=0' - 1 7/8"; R=0' - 1 15/16"; R+R=0' - 3 7/8"; R/2=0' - 0 31/32"; S=2' - 4 5/16"; T=1' - 2 5/32"; Type Comments=Airfoil Centrifugal Blower Counter-Clockwise Down Blast Arrangement 3 Class 2; U=0' - 11"; V=1' - 6"; W=0' - 0 11/16"; W/2=0' - 0 11/32"; X=2' - 6 5/16"; X/2=1' - 3 5/32"
- 180_CA-DWDI_CCW_DBD_CLASS_3: ((B+.25")/2)=1' - 1 5/32"; (D-A-.25)/2=0' - 1 9/16"; (G/5*3)+2"=1' - 0 11/32"; (M-(B+.25"))/2=0' - 1 7/8"; -((B+.25")/2)=-1' - 1 5/32"; -B/2=-1' - 1 1/32"; -P=-3' - 4 1/16"; A=1' - 6 1/2"; A+.25"=1' - 6 3/4"; A+.25"+DB_H=1' - 8 3/4"; A/2=0' - 9 1/4"; B=2' - 2 1/16"; B+.25"=2' - 2 5/16"; B/2=1' - 1 1/32"; D=1' - 9 7/8"; D/2=0' - 10 15/16"; DB_D=2' - 11 1/8"; DB_E=1' - 6"; DB_F=3' - 1 1/8"; DB_G=1' - 9 9/16"; DB_H=0' - 2"; E=2' - 5 7/16"; E/2=1' - 2 23/32"; F=2' - 9 1/2"; F-((D-A)/2)=2' - 7 13/16"; F-.125"=2' - 9 3/8"; G=1' - 6"; G+((G/5*3)+2")=2' - 6 11/32"; G-(G/5*3)=0' - 6 21/32"; G-2.5"=1' - 3 9/16"; G/10*3=0' - 5 11/16"; G/5*3=0' - 11 11/32"; H=3' - 1 1/8"; INLET=1' - 10 11/16"; INLET/2=0' - 11 11/32"; J=1' - 3 9/16"; K=0' - 2"; L=1' - 3 1/32"; M=2' - 6 1/16"; M/2=1' - 3 1/32"; N=0' - 7 3/4"; P=3' - 4 1/16"; P-N=-2' - 8 5/16"; P-N-M=0' - 2 1/4"; R=0' - 2 7/16"; R+R=0' - 4 7/8"; R/2=0' - 1 7/32"; S=2' - 4 5/16"; T=1' - 2 5/32"; Type Comments=Airfoil Centrifugal Blower Counter-Clockwise Down Blast Arrangement 3 Class 3; U=0' - 11"; V=1' - 6"; W=0' - 0 11/16"; W/2=0' - 0 11/32"; X=2' - 6 5/16"; X/2=1' - 3 5/32"
- 195_CA-DWDI_CCW_DBD_CLASS_2: ((B+.25")/2)=1' - 2 11/32"; (D-A-.25)/2=0' - 1 9/16"; (G/5*3)+2"=1' - 1 3/32"; (M-(B+.25"))/2=0' - 1 7/8"; -((B+.25")/2)=-1' - 2 11/32"; -B/2=-1' - 2 7/32"; -P=-3' - 6 3/16"; A=1' - 7 1/2"; A+.25"=1' - 7 3/4"; A+.25"+DB_H=1' - 9 3/4"; A/2=0' - 9 3/4"; B=2' - 4 7/16"; B+.25"=2' - 4 11/16"; B/2=1' - 2 7/32"; D=1' - 10 7/8"; D/2=0' - 11 7/16"; DB_D=3' - 2 1/2"; DB_E=1' - 8"; DB_F=3' - 4"; DB_G=1' - 11 3/16"; DB_H=0' - 2"; E=2' - 7 13/16"; E/2=1' - 3 29/32"; F=3' - 0 13/16"; F-((D-A)/2)=2' - 11 1/8"; F-.125"=3' - 0 11/16"; G=1' - 8"; G+((G/5*3)+2")=2' - 9 3/32"; G-(G/5*3)=0' - 7 29/32"; G-2.5"=1' - 5 13/16"; G/10*3=0' - 6 1/16"; G/5*3=1' - 0 3/32"; H=3' - 4"; INLET=2' - 0 3/16"; INLET/2=1' - 0 3/32"; J=1' - 4 13/16"; K=0' - 2"; L=1' - 4 7/32"; M=2' - 8 7/16"; M/2=1' - 4 7/32"; N=0' - 7 5/8"; P=3' - 6 3/16"; P-N=-2' - 10 9/16"; P-N-M=0' - 2 1/8"; R=0' - 2 3/16"; R+R=0' - 4 3/8"; R/2=0' - 1 3/32"; S=2' - 6 11/16"; T=1' - 3 11/32"; Type Comments=Airfoil Centrifugal Blower Counter-Clockwise Down Blast Arrangement 3 Class 2; U=0' - 11 1/2"; V=0' - 6"; W=0' - 0 11/16"; W/2=0' - 0 11/32"; X=2' - 8 11/16"; X/2=1' - 4 11/32"
- 195_CA-DWDI_CCW_DBD_CLASS_3: ((B+.25")/2)=1' - 2 11/32"; (D-A-.25)/2=0' - 1 9/16"; (G/5*3)+2"=1' - 1 3/32"; (M-(B+.25"))/2=0' - 1 7/8"; -((B+.25")/2)=-1' - 2 11/32"; -B/2=-1' - 2 7/32"; -P=-3' - 6 15/16"; A=1' - 7 1/2"; A+.25"=1' - 7 3/4"; A+.25"+DB_H=1' - 9 3/4"; A/2=0' - 9 3/4"; B=2' - 4 7/16"; B+.25"=2' - 4 11/16"; B/2=1' - 2 7/32"; D=1' - 10 7/8"; D/2=0' - 11 7/16"; DB_D=3' - 2 1/2"; DB_E=1' - 8"; DB_F=3' - 4"; DB_G=1' - 11 3/16"; DB_H=0' - 2"; E=2' - 7 13/16"; E/2=1' - 3 29/32"; F=3' - 0 13/16"; F-((D-A)/2)=2' - 11 1/8"; F-.125"=3' - 0 11/16"; G=1' - 8"; G+((G/5*3)+2")=2' - 9 3/32"; G-(G/5*3)=0' - 7 29/32"; G-2.5"=1' - 5 5/16"; G/10*3=0' - 6 1/16"; G/5*3=1' - 0 3/32"; H=3' - 4"; INLET=2' - 0 3/16"; INLET/2=1' - 0 3/32"; J=1' - 4 13/16"; K=0' - 2"; L=1' - 4 7/32"; M=2' - 8 7/16"; M/2=1' - 4 7/32"; N=0' - 8"; P=3' - 6 15/16"; P-N=-2' - 10 15/16"; P-N-M=0' - 2 1/2"; R=0' - 2 11/16"; R+R=0' - 5 3/8"; R/2=0' - 1 11/32"; S=2' - 6 11/16"; T=1' - 3 11/32"; Type Comments=Airfoil Centrifugal Blower Counter-Clockwise Down Blast Arrangement 3 Class 3; U=0' - 11 1/2"; V=0' - 6"; W=0' - 0 11/16"; W/2=0' - 0 11/32"; X=2' - 8 11/16"; X/2=1' - 4 11/32"
- 210_CA-DWDI_CCW_DBD_CLASS_2: ((B+.25")/2)=1' - 3 5/16"; (D-A-.25)/2=0' - 1 9/16"; (G/5*3)+2"=1' - 1 31/32"; (M-(B+.25"))/2=0' - 1 7/8"; -((B+.25")/2)=-1' - 3 5/16"; -B/2=-1' - 3 3/16"; -P=-3' - 8 5/8"; A=1' - 9 5/8"; A+.25"=1' - 9 7/8"; A+.25"+DB_H=1' - 11 7/8"; A/2=0' - 10 13/16"; B=2' - 6 3/8"; B+.25"=2' - 6 5/8"; B/2=1' - 3 3/16"; D=2' - 1"; D/2=1' - 0 1/2"; DB_D=3' - 4 15/16"; DB_E=1' - 9"; DB_F=3' - 6 7/8"; DB_G=2' - 0 7/8"; DB_H=0' - 2"; E=2' - 9 3/4"; E/2=1' - 4 7/8"; F=3' - 3 1/8"; F-((D-A)/2)=3' - 1 7/16"; F-.125"=3' - 3"; G=1' - 9"; G+((G/5*3)+2")=2' - 10 31/32"; G-(G/5*3)=0' - 8 1/32"; G-2.5"=1' - 6 13/16"; G/10*3=0' - 6 1/2"; G/5*3=1' - 0 31/32"; H=3' - 6 7/8"; INLET=2' - 1 15/16"; INLET/2=1' - 0 31/32"; J=1' - 6"; K=0' - 2"; L=1' - 5 3/16"; M=2' - 10 3/8"; M/2=1' - 5 3/16"; N=0' - 8 1/8"; P=3' - 8 5/8"; P-N=-3' - 0 1/2"; P-N-M=0' - 2 1/8"; R=0' - 2 3/16"; R+R=0' - 4 3/8"; R/2=0' - 1 3/32"; S=2' - 8 5/8"; T=1' - 4 5/16"; Type Comments=Airfoil Centrifugal Blower Counter-Clockwise Down Blast Arrangement 3 Class 2; U=1' - 0"; V=0' - 7"; W=0' - 0 13/16"; W/2=0' - 0 13/32"; X=2' - 10 5/8"; X/2=1' - 5 5/16"
- 210_CA-DWDI_CCW_DBD_CLASS_3: ((B+.25")/2)=1' - 3 5/16"; (D-A-.25)/2=0' - 1 9/16"; (G/5*3)+2"=1' - 1 31/32"; (M-(B+.25"))/2=0' - 1 7/8"; -((B+.25")/2)=-1' - 3 5/16"; -B/2=-1' - 3 3/16"; -P=-3' - 9 3/8"; A=1' - 9 5/8"; A+.25"=1' - 9 7/8"; A+.25"+DB_H=1' - 11 7/8"; A/2=0' - 10 13/16"; B=2' - 6 3/8"; B+.25"=2' - 6 5/8"; B/2=1' - 3 3/16"; D=2' - 1"; D/2=1' - 0 1/2"; DB_D=3' - 4 15/16"; DB_E=1' - 9"; DB_F=3' - 6 7/8"; DB_G=2' - 0 7/8"; DB_H=0' - 2"; E=2' - 9 3/4"; E/2=1' - 4 7/8"; F=3' - 3 1/8"; F-((D-A)/2)=3' - 1 7/16"; F-.125"=3' - 3"; G=1' - 9"; G+((G/5*3)+2")=2' - 10 31/32"; G-(G/5*3)=0' - 8 1/32"; G-2.5"=1' - 6 5/16"; G/10*3=0' - 6 1/2"; G/5*3=1' - 0 31/32"; H=3' - 6 7/8"; INLET=2' - 1 15/16"; INLET/2=1' - 0 31/32"; J=1' - 6"; K=0' - 2"; L=1' - 5 3/16"; M=2' - 10 3/8"; M/2=1' - 5 3/16"; N=0' - 8 1/2"; P=3' - 9 3/8"; P-N=-3' - 0 7/8"; P-N-M=0' - 2 1/2"; R=0' - 2 11/16"; R+R=0' - 5 3/8"; R/2=0' - 1 11/32"; S=2' - 8 5/8"; T=1' - 4 5/16"; Type Comments=Airfoil Centrifugal Blower Counter-Clockwise Down Blast Arrangement 3 Class 3; U=1' - 0"; V=0' - 7"; W=0' - 0 13/16"; W/2=0' - 0 13/32"; X=2' - 10 5/8"; X/2=1' - 5 5/16"
- 225_CA-DWDI_CCW_DBD_CLASS_2: ((B+.25")/2)=1' - 4 3/8"; (D-A-.25)/2=0' - 1 9/16"; (G/5*3)+2"=1' - 2 23/32"; (M-(B+.25"))/2=0' - 1 7/8"; -((B+.25")/2)=-1' - 4 3/8"; -B/2=-1' - 4 1/4"; -P=-3' - 11"; A=1' - 11 3/16"; A+.25"=1' - 11 7/16"; A+.25"+DB_H=2' - 1 7/16"; A/2=0' - 11 19/32"; B=2' - 8 1/2"; B+.25"=2' - 8 3/4"; B/2=1' - 4 1/4"; D=2' - 2 9/16"; D/2=1' - 1 9/32"; DB_D=3' - 8 3/8"; DB_E=1' - 11"; DB_F=3' - 9 3/4"; DB_G=2' - 2 1/2"; DB_H=0' - 2"; E=2' - 11 7/8"; E/2=1' - 5 15/16"; F=3' - 6 3/8"; F-((D-A)/2)=3' - 4 11/16"; F-.125"=3' - 6 1/4"; G=1' - 11"; G+((G/5*3)+2")=3' - 1 23/32"; G-(G/5*3)=0' - 9 9/32"; G-2.5"=1' - 8 9/16"; G/10*3=0' - 6 7/8"; G/5*3=1' - 1 23/32"; H=3' - 9 3/4"; INLET=2' - 3 7/16"; INLET/2=1' - 1 23/32"; J=1' - 7 1/4"; K=0' - 2"; L=1' - 6 1/4"; M=3' - 0 1/2"; M/2=1' - 6 1/4"; N=0' - 8 1/4"; P=3' - 11"; P-N=-3' - 2 3/4"; P-N-M=0' - 2 1/4"; R=0' - 2 7/16"; R+R=0' - 4 7/8"; R/2=0' - 1 7/32"; S=2' - 10 3/4"; T=1' - 5 3/8"; Type Comments=Airfoil Centrifugal Blower Counter-Clockwise Down Blast Arrangement 3 Class 2; U=1' - 0 1/2"; V=0' - 7 1/2"; W=0' - 0 13/16"; W/2=0' - 0 13/32"; X=3' - 0 3/4"; X/2=1' - 6 3/8"
- 225_CA-DWDI_CCW_DBD_CLASS_3: ((B+.25")/2)=1' - 4 3/8"; (D-A-.25)/2=0' - 1 9/16"; (G/5*3)+2"=1' - 2 23/32"; (M-(B+.25"))/2=0' - 1 7/8"; -((B+.25")/2)=-1' - 4 3/8"; -B/2=-1' - 4 1/4"; -P=-3' - 11 1/2"; A=1' - 11 3/16"; A+.25"=1' - 11 7/16"; A+.25"+DB_H=2' - 1 7/16"; A/2=0' - 11 19/32"; B=2' - 8 1/2"; B+.25"=2' - 8 3/4"; B/2=1' - 4 1/4"; D=2' - 2 9/16"; D/2=1' - 1 9/32"; DB_D=3' - 8 3/8"; DB_E=1' - 11"; DB_F=3' - 9 3/4"; DB_G=2' - 2 1/2"; DB_H=0' - 2"; E=2' - 11 7/8"; E/2=1' - 5 15/16"; F=3' - 6 3/8"; F-((D-A)/2)=3' - 4 11/16"; F-.125"=3' - 6 1/4"; G=1' - 11"; G+((G/5*3)+2")=3' - 1 23/32"; G-(G/5*3)=0' - 9 9/32"; G-2.5"=1' - 8 1/16"; G/10*3=0' - 6 7/8"; G/5*3=1' - 1 23/32"; H=3' - 9 3/4"; INLET=2' - 3 7/16"; INLET/2=1' - 1 23/32"; J=1' - 7 1/4"; K=0' - 2"; L=1' - 6 1/4"; M=3' - 0 1/2"; M/2=1' - 6 1/4"; N=0' - 8 1/2"; P=3' - 11 1/2"; P-N=-3' - 3"; P-N-M=0' - 2 1/2"; R=0' - 2 15/16"; R+R=0' - 5 7/8"; R/2=0' - 1 15/32"; S=2' - 10 3/4"; T=1' - 5 3/8"; Type Comments=Airfoil Centrifugal Blower Counter-Clockwise Down Blast Arrangement 3 Class 3; U=1' - 0 1/2"; V=0' - 7 1/2"; W=0' - 0 13/16"; W/2=0' - 0 13/32"; X=3' - 0 3/4"; X/2=1' - 6 3/8"
- 245_CA-DWDI_CCW_DBD_CLASS_2: ((B+.25")/2)=1' - 5 21/32"; (D-A-.25)/2=0' - 1 9/16"; (G/5*3)+2"=1' - 3 23/32"; (M-(B+.25"))/2=0' - 1 7/8"; -((B+.25")/2)=-1' - 5 21/32"; -B/2=-1' - 5 17/32"; -P=-4' - 2 1/16"; A=2' - 1 1/2"; A+.25"=2' - 1 3/4"; A+.25"+DB_H=2' - 3 3/4"; A/2=1' - 0 3/4"; B=2' - 11 1/16"; B+.25"=2' - 11 5/16"; B/2=1' - 5 17/32"; D=2' - 4 7/8"; D/2=1' - 2 7/16"; DB_D=4' - 0 1/4"; DB_E=2' - 1"; DB_F=4' - 1 1/2"; DB_G=2' - 4 5/8"; DB_H=0' - 2"; E=3' - 2 7/16"; E/2=1' - 7 7/32"; F=3' - 10 1/8"; F-((D-A)/2)=3' - 8 7/16"; F-.125"=3' - 10"; G=2' - 1"; G+((G/5*3)+2")=3' - 4 23/32"; G-(G/5*3)=0' - 10 9/32"; G-2.5"=1' - 10 9/16"; G/10*3=0' - 7 3/8"; G/5*3=1' - 2 23/32"; H=4' - 1 1/2"; INLET=2' - 5 7/16"; INLET/2=1' - 2 23/32"; J=1' - 8 7/8"; K=0' - 2"; L=1' - 7 17/32"; M=3' - 3 1/16"; M/2=1' - 7 17/32"; N=0' - 8 3/4"; P=4' - 2 1/16"; P-N=-3' - 5 5/16"; P-N-M=0' - 2 1/4"; R=0' - 2 7/16"; R+R=0' - 4 7/8"; R/2=0' - 1 7/32"; S=3' - 1 5/16"; T=1' - 6 21/32"; Type Comments=Airfoil Centrifugal Blower Counter-Clockwise Down Blast Arrangement 3 Class 2; U=1' - 1 1/2"; V=0' - 8"; W=0' - 0 13/16"; W/2=0' - 0 13/32"; X=3' - 5 5/16"; X/2=1' - 8 21/32"
- 245_CA-DWDI_CCW_DBD_CLASS_3: ((B+.25")/2)=1' - 5 21/32"; (D-A-.25)/2=0' - 1 9/16"; (G/5*3)+2"=1' - 3 23/32"; (M-(B+.25"))/2=0' - 1 7/8"; -((B+.25")/2)=-1' - 5 21/32"; -B/2=-1' - 5 17/32"; -P=-4' - 2 11/16"; A=2' - 1 1/2"; A+.25"=2' - 1 3/4"; A+.25"+DB_H=2' - 3 3/4"; A/2=1' - 0 3/4"; B=2' - 11 1/16"; B+.25"=2' - 11 5/16"; B/2=1' - 5 17/32"; D=2' - 4 7/8"; D/2=1' - 2 7/16"; DB_D=4' - 0 1/4"; DB_E=2' - 1"; DB_F=4' - 1 1/2"; DB_G=2' - 4 5/8"; DB_H=0' - 2"; E=3' - 2 7/16"; E/2=1' - 7 7/32"; F=3' - 10 1/8"; F-((D-A)/2)=3' - 8 7/16"; F-.125"=3' - 10"; G=2' - 1"; G+((G/5*3)+2")=3' - 4 23/32"; G-(G/5*3)=0' - 10 9/32"; G-2.5"=1' - 10 13/16"; G/10*3=0' - 7 3/8"; G/5*3=1' - 2 23/32"; H=4' - 1 1/2"; INLET=2' - 5 7/16"; INLET/2=1' - 2 23/32"; J=1' - 8 7/8"; K=0' - 2"; L=1' - 7 17/32"; M=3' - 3 1/16"; M/2=1' - 7 17/32"; N=0' - 8 3/4"; P=4' - 2 11/16"; P-N=-3' - 5 15/16"; P-N-M=0' - 2 7/8"; R=0' - 2 3/16"; R+R=0' - 4 3/8"; R/2=0' - 1 3/32"; S=3' - 1 5/16"; T=1' - 6 21/32"; Type Comments=Airfoil Centrifugal Blower Counter-Clockwise Down Blast Arrangement 3 Class 3; U=1' - 1 1/2"; V=0' - 8"; W=0' - 0 13/16"; W/2=0' - 0 13/32"; X=3' - 5 5/16"; X/2=1' - 8 21/32"
- 270_CA-DWDI_CCW_DBD_CLASS_2: ((B+.25")/2)=1' - 7 27/32"; (D-A-.25)/2=0' - 1 9/16"; (G/5*3)+2"=1' - 4 31/32"; (M-(B+.25"))/2=0' - 1 7/8"; -((B+.25")/2)=-1' - 7 27/32"; -B/2=-1' - 7 23/32"; -P=-4' - 6 15/16"; A=2' - 3 1/2"; A+.25"=2' - 3 3/4"; A+.25"+DB_H=2' - 5 3/4"; A/2=1' - 1 3/4"; B=3' - 3 7/16"; B+.25"=3' - 3 11/16"; B/2=1' - 7 23/32"; D=2' - 6 7/8"; D/2=1' - 3 7/16"; DB_D=4' - 2 1/8"; DB_E=2' - 3"; DB_F=4' - 6 3/4"; DB_G=2' - 7 3/8"; DB_H=0' - 2"; E=3' - 6 13/16"; E/2=1' - 9 13/32"; F=4' - 2 1/4"; F-((D-A)/2)=4' - 0 9/16"; F-.125"=4' - 2 1/8"; G=2' - 3"; G+((G/5*3)+2")=3' - 7 31/32"; G-(G/5*3)=0' - 11 1/32"; G-2.5"=2' - 0 5/16"; G/10*3=0' - 8"; G/5*3=1' - 3 31/32"; H=4' - 6 3/4"; INLET=2' - 7 15/16"; INLET/2=1' - 3 31/32"; J=1' - 11 3/8"; K=0' - 2"; L=1' - 9 23/32"; M=3' - 7 7/16"; M/2=1' - 9 23/32"; N=0' - 9"; P=4' - 6 15/16"; P-N=-3' - 9 15/16"; P-N-M=0' - 2 1/2"; R=0' - 2 11/16"; R+R=0' - 5 3/8"; R/2=0' - 1 11/32"; S=3' - 5 11/16"; T=1' - 8 27/32"; Type Comments=Airfoil Centrifugal Blower Counter-Clockwise Down Blast Arrangement 3 Class 2; U=1' - 3"; V=0' - 9"; W=0' - 0 13/16"; W/2=0' - 0 13/32"; X=3' - 9 11/16"; X/2=1' - 10 27/32"
- 270_CA-DWDI_CCW_DBD_CLASS_3: ((B+.25")/2)=1' - 7 27/32"; (D-A-.25)/2=0' - 1 9/16"; (G/5*3)+2"=1' - 4 31/32"; (M-(B+.25"))/2=0' - 1 7/8"; -((B+.25")/2)=-1' - 7 27/32"; -B/2=-1' - 7 23/32"; -P=-4' - 7 1/16"; A=2' - 3 1/2"; A+.25"=2' - 3 3/4"; A+.25"+DB_H=2' - 5 3/4"; A/2=1' - 1 3/4"; B=3' - 3 7/16"; B+.25"=3' - 3 11/16"; B/2=1' - 7 23/32"; D=2' - 6 7/8"; D/2=1' - 3 7/16"; DB_D=4' - 2 1/8"; DB_E=2' - 3"; DB_F=4' - 6 3/4"; DB_G=2' - 7 3/8"; DB_H=0' - 2"; E=3' - 6 13/16"; E/2=1' - 9 13/32"; F=4' - 2 1/4"; F-((D-A)/2)=4' - 0 9/16"; F-.125"=4' - 2 1/8"; G=2' - 3"; G+((G/5*3)+2")=3' - 7 31/32"; G-(G/5*3)=0' - 11 1/32"; G-2.5"=2' - 0 13/16"; G/10*3=0' - 8"; G/5*3=1' - 3 31/32"; H=4' - 6 3/4"; INLET=2' - 7 15/16"; INLET/2=1' - 3 31/32"; J=1' - 11 3/8"; K=0' - 2"; L=1' - 9 23/32"; M=3' - 7 7/16"; M/2=1' - 9 23/32"; N=0' - 8 3/4"; P=4' - 7 1/16"; P-N=-3' - 10 5/16"; P-N-M=0' - 2 7/8"; R=0' - 2 3/16"; R+R=0' - 4 3/8"; R/2=0' - 1 3/32"; S=3' - 5 11/16"; T=1' - 8 27/32"; Type Comments=Airfoil Centrifugal Blower Counter-Clockwise Down Blast Arrangement 3 Class 3; U=1' - 3"; V=0' - 9"; W=0' - 0 13/16"; W/2=0' - 0 13/32"; X=3' - 9 11/16"; X/2=1' - 10 27/32"
- 300_CA-DWDI_CCW_DBD_CLASS_2: ((B+.25")/2)=1' - 9 5/8"; (D-A-.25)/2=0' - 1 19/32"; (G/5*3)+2"=1' - 6 15/32"; (M-(B+.25"))/2=0' - 1 7/8"; -((B+.25")/2)=-1' - 9 5/8"; -B/2=-1' - 9 1/2"; -P=-4' - 11"; A=2' - 7 3/16"; A+.25"=2' - 7 7/16"; A+.25"+DB_H=2' - 9 7/16"; A/2=1' - 3 19/32"; B=3' - 7"; B+.25"=3' - 7 1/4"; B/2=1' - 9 1/2"; D=2' - 10 5/8"; D/2=1' - 5 5/16"; DB_D=4' - 10 1/2"; DB_E=2' - 6"; DB_F=5' - 0"; DB_G=2' - 10 5/8"; DB_H=0' - 2"; E=3' - 10 7/16"; E/2=1' - 11 7/32"; F=4' - 7 7/8"; F-((D-A)/2)=4' - 6 5/32"; F-.125"=4' - 7 3/4"; G=2' - 6"; G+((G/5*3)+2")=4' - 0 15/32"; G-(G/5*3)=1' - 0 17/32"; G-2.5"=2' - 3 5/16"; G/10*3=0' - 8 3/4"; G/5*3=1' - 5 15/32"; H=5' - 0"; INLET=2' - 10 15/16"; INLET/2=1' - 5 15/32"; J=2' - 1 3/8"; K=0' - 2"; L=1' - 11 1/2"; M=3' - 11"; M/2=1' - 11 1/2"; N=0' - 9 1/2"; P=4' - 11"; P-N=-4' - 1 1/2"; P-N-M=0' - 2 1/2"; R=0' - 2 11/16"; R+R=0' - 5 3/8"; R/2=0' - 1 11/32"; S=3' - 9 1/4"; T=1' - 10 5/8"; Type Comments=Airfoil Centrifugal Blower Counter-Clockwise Down Blast Arrangement 3 Class 2; U=1' - 4 1/2"; V=0' - 10"; W=0' - 0 13/16"; W/2=0' - 0 13/32"; X=4' - 1 1/4"; X/2=2' - 0 5/8"
- 300_CA-DWDI_CCW_DBD_CLASS_3: ((B+.25")/2)=1' - 9 5/8"; (D-A-.25)/2=0' - 1 19/32"; (G/5*3)+2"=1' - 6 15/32"; (M-(B+.25"))/2=0' - 1 7/8"; -((B+.25")/2)=-1' - 9 5/8"; -B/2=-1' - 9 1/2"; -P=-4' - 11 3/8"; A=2' - 7 3/16"; A+.25"=2' - 7 7/16"; A+.25"+DB_H=2' - 9 7/16"; A/2=1' - 3 19/32"; B=3' - 7"; B+.25"=3' - 7 1/4"; B/2=1' - 9 1/2"; D=2' - 10 5/8"; D/2=1' - 5 5/16"; DB_D=4' - 10 1/2"; DB_E=2' - 6"; DB_F=5' - 0"; DB_G=2' - 10 5/8"; DB_H=0' - 2"; E=3' - 10 7/16"; E/2=1' - 11 7/32"; F=4' - 7 7/8"; F-((D-A)/2)=4' - 6 5/32"; F-.125"=4' - 7 3/4"; G=2' - 6"; G+((G/5*3)+2")=4' - 0 15/32"; G-(G/5*3)=1' - 0 17/32"; G-2.5"=2' - 3 9/16"; G/10*3=0' - 8 3/4"; G/5*3=1' - 5 15/32"; H=5' - 0"; INLET=2' - 10 15/16"; INLET/2=1' - 5 15/32"; J=2' - 1 3/8"; K=0' - 2"; L=1' - 11 1/2"; M=3' - 11"; M/2=1' - 11 1/2"; N=0' - 9 1/2"; P=4' - 11 3/8"; P-N=-4' - 1 7/8"; P-N-M=0' - 2 7/8"; R=0' - 2 7/16"; R+R=0' - 4 7/8"; R/2=0' - 1 7/32"; S=3' - 9 1/4"; T=1' - 10 5/8"; Type Comments=Airfoil Centrifugal Blower Counter-Clockwise Down Blast Arrangement 3 Class 3; U=1' - 4 1/2"; V=0' - 10"; W=0' - 0 13/16"; W/2=0' - 0 13/32"; X=4' - 1 1/4"; X/2=2' - 0 5/8"
- 330_CA-DWDI_CCW_DBD_CLASS_2: ((B+.25")/2)=1' - 11 21/32"; (D-A-.25)/2=0' - 2 3/32"; (G/5*3)+2"=1' - 7 31/32"; (M-(B+.25"))/2=0' - 1 7/8"; -((B+.25")/2)=-1' - 11 21/32"; -B/2=-1' - 11 17/32"; -P=-5' - 3 11/16"; A=2' - 10 1/2"; A+.25"=2' - 10 3/4"; A+.25"+DB_H=3' - 0 3/4"; A/2=1' - 5 1/4"; B=3' - 11 1/16"; B+.25"=3' - 11 5/16"; B/2=1' - 11 17/32"; D=3' - 2 15/16"; D/2=1' - 7 15/32"; DB_D=5' - 4 3/8"; DB_E=2' - 9"; DB_F=5' - 5 3/4"; DB_G=3' - 1 7/8"; DB_H=0' - 2"; E=4' - 3 1/2"; E/2=2' - 1 3/4"; F=5' - 1 3/8"; F-((D-A)/2)=4' - 11 5/32"; F-.125"=5' - 1 1/4"; G=2' - 9"; G+((G/5*3)+2")=4' - 4 31/32"; G-(G/5*3)=1' - 2 1/32"; G-2.5"=2' - 6 13/16"; G/10*3=0' - 9 1/2"; G/5*3=1' - 6 31/32"; H=5' - 5 3/4"; INLET=3' - 1 15/16"; INLET/2=1' - 6 31/32"; J=2' - 3 7/8"; K=0' - 2"; L=2' - 1 17/32"; M=4' - 3 1/16"; M/2=2' - 1 17/32"; N=0' - 9 5/8"; P=5' - 3 11/16"; P-N=-4' - 6 1/16"; P-N-M=0' - 3"; R=0' - 2 3/16"; R+R=0' - 4 3/8"; R/2=0' - 1 3/32"; S=4' - 1 5/16"; T=2' - 0 21/32"; Type Comments=Airfoil Centrifugal Blower Counter-Clockwise Down Blast Arrangement 3 Class 2; U=1' - 6"; V=1' - 0"; W=0' - 0 13/16"; W/2=0' - 0 13/32"; X=4' - 5 7/16"; X/2=2' - 2 23/32"
- 330_CA-DWDI_CCW_DBD_CLASS_3: ((B+.25")/2)=1' - 11 21/32"; (D-A-.25)/2=0' - 2 3/32"; (G/5*3)+2"=1' - 7 31/32"; (M-(B+.25"))/2=0' - 1 7/8"; -((B+.25")/2)=-1' - 11 21/32"; -B/2=-1' - 11 17/32"; -P=-5' - 3 15/16"; A=2' - 10 1/2"; A+.25"=2' - 10 3/4"; A+.25"+DB_H=3' - 0 3/4"; A/2=1' - 5 1/4"; B=3' - 11 1/16"; B+.25"=3' - 11 5/16"; B/2=1' - 11 17/32"; D=3' - 2 15/16"; D/2=1' - 7 15/32"; DB_D=5' - 4 3/8"; DB_E=2' - 9"; DB_F=5' - 5 3/4"; DB_G=3' - 1 7/8"; DB_H=0' - 2"; E=4' - 3 1/2"; E/2=2' - 1 3/4"; F=5' - 1 3/8"; F-((D-A)/2)=4' - 11 5/32"; F-.125"=5' - 1 1/4"; G=2' - 9"; G+((G/5*3)+2")=4' - 4 31/32"; G-(G/5*3)=1' - 2 1/32"; G-2.5"=2' - 6 9/16"; G/10*3=0' - 9 1/2"; G/5*3=1' - 6 31/32"; H=5' - 5 3/4"; INLET=3' - 1 15/16"; INLET/2=1' - 6 31/32"; J=2' - 3 7/8"; K=0' - 2"; L=2' - 1 17/32"; M=4' - 3 1/16"; M/2=2' - 1 17/32"; N=0' - 10"; P=5' - 3 15/16"; P-N=-4' - 5 15/16"; P-N-M=0' - 2 7/8"; R=0' - 2 7/16"; R+R=0' - 4 7/8"; R/2=0' - 1 7/32"; S=4' - 1 5/16"; T=2' - 0 21/32"; Type Comments=Airfoil Centrifugal Blower Counter-Clockwise Down Blast Arrangement 3 Class 3; U=1' - 6"; V=1' - 0"; W=0' - 0 13/16"; W/2=0' - 0 13/32"; X=4' - 5 7/16"; X/2=2' - 2 23/32"
- 365_CA-DWDI_CCW_DBD_CLASS_2: ((B+.25")/2)=2' - 2 7/32"; (D-A-.25)/2=0' - 2 3/32"; (G/5*3)+2"=1' - 9 23/32"; (M-(B+.25"))/2=0' - 1 7/8"; -((B+.25")/2)=-2' - 2 7/32"; -B/2=-2' - 2 3/32"; -P=-5' - 9 9/16"; A=3' - 2 11/16"; A+.25"=3' - 2 15/16"; A+.25"+DB_H=3' - 4 15/16"; A/2=1' - 7 11/32"; B=4' - 4 3/16"; B+.25"=4' - 4 7/16"; B/2=2' - 2 3/32"; D=3' - 7 1/8"; D/2=1' - 9 9/16"; DB_D=5' - 10 5/8"; DB_E=3' - 0"; DB_F=6' - 0 3/8"; DB_G=3' - 5 3/4"; DB_H=0' - 2"; E=4' - 8 5/8"; E/2=2' - 4 5/16"; F=5' - 7 7/16"; F-((D-A)/2)=5' - 5 7/32"; F-.125"=5' - 7 5/16"; G=3' - 0"; G+((G/5*3)+2")=4' - 9 23/32"; G-(G/5*3)=1' - 3 9/32"; G-2.5"=2' - 9 9/16"; G/10*3=0' - 10 3/8"; G/5*3=1' - 8 23/32"; H=6' - 0 3/8"; INLET=3' - 5 7/16"; INLET/2=1' - 8 23/32"; J=2' - 6 5/8"; K=0' - 2"; L=2' - 4 3/32"; M=4' - 8 3/16"; M/2=2' - 4 3/32"; N=0' - 10 1/2"; P=5' - 9 9/16"; P-N=-4' - 11 1/16"; P-N-M=0' - 2 7/8"; R=0' - 2 7/16"; R+R=0' - 4 7/8"; R/2=0' - 1 7/32"; S=4' - 6 7/16"; T=2' - 3 7/32"; Type Comments=Airfoil Centrifugal Blower Counter-Clockwise Down Blast Arrangement 3 Class 2; U=1' - 8"; V=1' - 1"; W=0' - 0 13/16"; W/2=0' - 0 13/32"; X=4' - 10 9/16"; X/2=2' - 5 9/32"
- 365_CA-DWDI_CCW_DBD_CLASS_3: ((B+.25")/2)=2' - 2 7/32"; (D-A-.25)/2=0' - 2 3/32"; (G/5*3)+2"=1' - 9 23/32"; (M-(B+.25"))/2=0' - 1 7/8"; -((B+.25")/2)=-2' - 2 7/32"; -B/2=-2' - 2 3/32"; -P=-5' - 10 1/16"; A=3' - 2 11/16"; A+.25"=3' - 2 15/16"; A+.25"+DB_H=3' - 4 15/16"; A/2=1' - 7 11/32"; B=4' - 4 3/16"; B+.25"=4' - 4 7/16"; B/2=2' - 2 3/32"; D=3' - 7 1/8"; D/2=1' - 9 9/16"; DB_D=5' - 10 5/8"; DB_E=3' - 0"; DB_F=6' - 0 3/8"; DB_G=3' - 5 3/4"; DB_H=0' - 2"; E=4' - 8 5/8"; E/2=2' - 4 5/16"; F=5' - 7 7/16"; F-((D-A)/2)=5' - 5 7/32"; F-.125"=5' - 7 5/16"; G=3' - 0"; G+((G/5*3)+2")=4' - 9 23/32"; G-(G/5*3)=1' - 3 9/32"; G-2.5"=2' - 9 5/16"; G/10*3=0' - 10 3/8"; G/5*3=1' - 8 23/32"; H=6' - 0 3/8"; INLET=3' - 5 7/16"; INLET/2=1' - 8 23/32"; J=2' - 6 5/8"; K=0' - 2"; L=2' - 4 3/32"; M=4' - 8 3/16"; M/2=2' - 4 3/32"; N=0' - 10 1/2"; P=5' - 10 1/16"; P-N=-4' - 11 9/16"; P-N-M=0' - 3 3/8"; R=0' - 2 11/16"; R+R=0' - 5 3/8"; R/2=0' - 1 11/32"; S=4' - 6 7/16"; T=2' - 3 7/32"; Type Comments=Airfoil Centrifugal Blower Counter-Clockwise Down Blast Arrangement 3 Class 3; U=1' - 8"; V=1' - 1"; W=0' - 0 13/16"; W/2=0' - 0 13/32"; X=4' - 10 9/16"; X/2=2' - 5 9/32"
- 402_CA-DWDI_CCW_DBD_CLASS_2: ((B+.25")/2)=2' - 5 1/32"; (D-A-.25)/2=0' - 2 3/32"; (G/5*3)+2"=1' - 11 19/32"; (M-(B+.25"))/2=0' - 2 7/8"; -((B+.25")/2)=-2' - 5 1/32"; -B/2=-2' - 4 29/32"; -P=-6' - 3 11/16"; A=3' - 5 3/4"; A+.25"=3' - 6"; A+.25"+DB_H=3' - 9"; A/2=1' - 8 7/8"; B=4' - 9 13/16"; B+.25"=4' - 10 1/16"; B/2=2' - 4 29/32"; D=3' - 10 3/16"; D/2=1' - 11 3/32"; DB_D=6' - 6 1/4"; DB_E=3' - 4"; DB_F=6' - 8 3/8"; DB_G=3' - 10 3/4"; DB_H=0' - 3"; E=5' - 2 1/4"; E/2=2' - 7 1/8"; F=6' - 2 11/16"; F-((D-A)/2)=6' - 0 15/32"; F-.125"=6' - 2 9/16"; G=3' - 4"; G+((G/5*3)+2")=5' - 3 19/32"; G-(G/5*3)=1' - 5 13/32"; G-2.5"=3' - 1 9/16"; G/10*3=0' - 11 5/16"; G/5*3=1' - 10 19/32"; H=6' - 8 3/8"; INLET=3' - 9 3/16"; INLET/2=1' - 10 19/32"; J=2' - 9 5/8"; K=0' - 3"; L=2' - 7 29/32"; M=5' - 3 13/16"; M/2=2' - 7 29/32"; N=0' - 10"; P=6' - 3 11/16"; P-N=-5' - 5 11/16"; P-N-M=0' - 1 7/8"; R=0' - 2 7/16"; R+R=0' - 4 7/8"; R/2=0' - 1 7/32"; S=5' - 1 5/16"; T=2' - 6 21/32"; Type Comments=Airfoil Centrifugal Blower Counter-Clockwise Down Blast Arrangement 3 Class 2; U=1' - 10"; V=1' - 2"; W=0' - 1 1/16"; W/2=0' - 0 17/32"; X=5' - 5 3/16"; X/2=2' - 8 19/32"
- 402_CA-DWDI_CCW_DBD_CLASS_3: ((B+.25")/2)=2' - 5 1/32"; (D-A-.25)/2=0' - 2 3/32"; (G/5*3)+2"=1' - 11 19/32"; (M-(B+.25"))/2=0' - 2 7/8"; -((B+.25")/2)=-2' - 5 1/32"; -B/2=-2' - 4 29/32"; -P=-6' - 4 3/16"; A=3' - 5 3/4"; A+.25"=3' - 6"; A+.25"+DB_H=3' - 9"; A/2=1' - 8 7/8"; B=4' - 9 13/16"; B+.25"=4' - 10 1/16"; B/2=2' - 4 29/32"; D=3' - 10 3/16"; D/2=1' - 11 3/32"; DB_D=6' - 6 1/4"; DB_E=3' - 4"; DB_F=6' - 8 3/8"; DB_G=3' - 10 3/4"; DB_H=0' - 3"; E=5' - 2 1/4"; E/2=2' - 7 1/8"; F=6' - 2 11/16"; F-((D-A)/2)=6' - 0 15/32"; F-.125"=6' - 2 9/16"; G=3' - 4"; G+((G/5*3)+2")=5' - 3 19/32"; G-(G/5*3)=1' - 5 13/32"; G-2.5"=3' - 1 5/16"; G/10*3=0' - 11 5/16"; G/5*3=1' - 10 19/32"; H=6' - 8 3/8"; INLET=3' - 9 3/16"; INLET/2=1' - 10 19/32"; J=2' - 9 5/8"; K=0' - 3"; L=2' - 7 29/32"; M=5' - 3 13/16"; M/2=2' - 7 29/32"; N=0' - 10 1/2"; P=6' - 4 3/16"; P-N=-5' - 5 11/16"; P-N-M=0' - 1 7/8"; R=0' - 2 11/16"; R+R=0' - 5 3/8"; R/2=0' - 1 11/32"; S=5' - 1 5/16"; T=2' - 6 21/32"; Type Comments=Airfoil Centrifugal Blower Counter-Clockwise Down Blast Arrangement 3 Class 3; U=1' - 10"; V=1' - 2"; W=0' - 1 1/16"; W/2=0' - 0 17/32"; X=5' - 5 3/16"; X/2=2' - 8 19/32"
- 445_CA-DWDI_CCW_DBD_CLASS_2: ((B+.25")/2)=2' - 8 1/4"; (D-A-.25)/2=0' - 2 3/32"; (G/5*3)+2"=2' - 1 23/32"; (M-(B+.25"))/2=0' - 2 7/8"; -((B+.25")/2)=-2' - 8 1/4"; -B/2=-2' - 8 1/8"; -P=-6' - 11 1/2"; A=3' - 9 15/16"; A+.25"=3' - 10 3/16"; A+.25"+DB_H=4' - 1 3/16"; A/2=1' - 10 31/32"; B=5' - 4 1/4"; B+.25"=5' - 4 1/2"; B/2=2' - 8 1/8"; D=4' - 2 3/8"; D/2=2' - 1 3/16"; DB_D=7' - 2 1/4"; DB_E=3' - 8"; DB_F=7' - 4 1/2"; DB_G=4' - 3 3/8"; DB_H=0' - 3"; E=5' - 8 11/16"; E/2=2' - 10 11/32"; F=6' - 10 5/16"; F-((D-A)/2)=6' - 8 3/32"; F-.125"=6' - 10 3/16"; G=3' - 8"; G+((G/5*3)+2")=5' - 9 23/32"; G-(G/5*3)=1' - 7 9/32"; G-2.5"=3' - 5 5/16"; G/10*3=1' - 0 3/8"; G/5*3=2' - 0 23/32"; H=7' - 4 1/2"; INLET=4' - 1 7/16"; INLET/2=2' - 0 23/32"; J=3' - 1 1/8"; K=0' - 3"; L=2' - 11 1/8"; M=5' - 10 1/4"; M/2=2' - 11 1/8"; N=0' - 11"; P=6' - 11 1/2"; P-N=-6' - 0 1/2"; P-N-M=0' - 2 1/4"; R=0' - 2 11/16"; R+R=0' - 5 3/8"; R/2=0' - 1 11/32"; S=5' - 7 3/4"; T=2' - 9 7/8"; Type Comments=Airfoil Centrifugal Blower Counter-Clockwise Down Blast Arrangement 3 Class 2; U=2' - 0"; V=1' - 4"; W=0' - 1 1/16"; W/2=0' - 0 17/32"; X=5' - 11 5/8"; X/2=2' - 11 13/16"
- 445_CA-DWDI_CCW_DBD_CLASS_3: ((B+.25")/2)=2' - 8 1/4"; (D-A-.25)/2=0' - 2 3/32"; (G/5*3)+2"=2' - 1 23/32"; (M-(B+.25"))/2=0' - 2 7/8"; -((B+.25")/2)=-2' - 8 1/4"; -B/2=-2' - 8 1/8"; -P=-6' - 11 1/2"; A=3' - 9 15/16"; A+.25"=3' - 10 3/16"; A+.25"+DB_H=4' - 1 3/16"; A/2=1' - 10 31/32"; B=5' - 4 1/4"; B+.25"=5' - 4 1/2"; B/2=2' - 8 1/8"; D=4' - 2 3/8"; D/2=2' - 1 3/16"; DB_D=7' - 2 1/4"; DB_E=3' - 8"; DB_F=7' - 4 1/2"; DB_G=4' - 3 3/8"; DB_H=0' - 3"; E=5' - 8 11/16"; E/2=2' - 10 11/32"; F=6' - 10 5/16"; F-((D-A)/2)=6' - 8 3/32"; F-.125"=6' - 10 3/16"; G=3' - 8"; G+((G/5*3)+2")=5' - 9 23/32"; G-(G/5*3)=1' - 7 9/32"; G-2.5"=3' - 5 1/16"; G/10*3=1' - 0 3/8"; G/5*3=2' - 0 23/32"; H=7' - 4 1/2"; INLET=4' - 1 7/16"; INLET/2=2' - 0 23/32"; J=3' - 1 1/8"; K=0' - 3"; L=2' - 11 1/8"; M=5' - 10 1/4"; M/2=2' - 11 1/8"; N=0' - 11"; P=6' - 11 1/2"; P-N=-6' - 0 1/2"; P-N-M=0' - 2 1/4"; R=0' - 2 15/16"; R+R=0' - 5 7/8"; R/2=0' - 1 15/32"; S=5' - 7 3/4"; T=2' - 9 7/8"; Type Comments=Airfoil Centrifugal Blower Counter-Clockwise Down Blast Arrangement 3 Class 3; U=2' - 0"; V=1' - 4"; W=0' - 1 1/16"; W/2=0' - 0 17/32"; X=5' - 11 5/8"; X/2=2' - 11 13/16"
- 490_CA-DWDI_CCW_DBD_CLASS_2: ((B+.25")/2)=2' - 11 3/16"; (D-A-.25)/2=0' - 2 3/32"; (G/5*3)+2"=2' - 4 1/2"; (M-(B+.25"))/2=0' - 2 7/8"; -((B+.25")/2)=-2' - 11 3/16"; -B/2=-2' - 11 1/16"; -P=-7' - 6 3/8"; A=4' - 3"; A+.25"=4' - 3 1/4"; A+.25"+DB_H=4' - 6 1/4"; A/2=2' - 1 1/2"; B=5' - 10 1/8"; B+.25"=5' - 10 3/8"; B/2=2' - 11 1/16"; D=4' - 7 7/16"; D/2=2' - 3 23/32"; DB_D=7' - 10 1/2"; DB_E=4' - 0"; DB_F=8' - 1"; DB_G=4' - 8 1/4"; DB_H=0' - 3"; E=6' - 2 9/16"; E/2=3' - 1 9/32"; F=7' - 6 3/16"; F-((D-A)/2)=7' - 3 31/32"; F-.125"=7' - 6 1/16"; G=4' - 0"; G+((G/5*3)+2")=6' - 4 1/2"; G-(G/5*3)=1' - 8 1/2"; G-2.5"=3' - 8 9/16"; G/10*3=1' - 1 3/4"; G/5*3=2' - 3 1/2"; H=8' - 1"; INLET=4' - 7"; INLET/2=2' - 3 1/2"; J=3' - 4 3/4"; K=0' - 3"; L=3' - 2 1/16"; M=6' - 4 1/8"; M/2=3' - 2 1/16"; N=1' - 0"; P=7' - 6 3/8"; P-N=-6' - 6 3/8"; P-N-M=0' - 2 1/4"; R=0' - 3 7/16"; R+R=0' - 6 7/8"; R/2=0' - 1 23/32"; S=6' - 1 5/8"; T=3' - 0 13/16"; Type Comments=Airfoil Centrifugal Blower Counter-Clockwise Down Blast Arrangement 3 Class 2; U=2' - 2 1/2"; V=1' - 6"; W=0' - 1 1/16"; W/2=0' - 0 17/32"; X=6' - 5 1/2"; X/2=3' - 2 3/4"
- 490_CA-DWDI_CCW_DBD_CLASS_3: ((B+.25")/2)=2' - 11 3/16"; (D-A-.25)/2=0' - 2 3/32"; (G/5*3)+2"=2' - 4 1/2"; (M-(B+.25"))/2=0' - 2 7/8"; -((B+.25")/2)=-2' - 11 3/16"; -B/2=-2' - 11 1/16"; -P=-7' - 6 5/8"; A=4' - 3"; A+.25"=4' - 3 1/4"; A+.25"+DB_H=4' - 6 1/4"; A/2=2' - 1 1/2"; B=5' - 10 1/8"; B+.25"=5' - 10 3/8"; B/2=2' - 11 1/16"; D=4' - 7 7/16"; D/2=2' - 3 23/32"; DB_D=7' - 10 1/2"; DB_E=4' - 0"; DB_F=8' - 1"; DB_G=4' - 8 1/4"; DB_H=0' - 3"; E=6' - 2 9/16"; E/2=3' - 1 9/32"; F=7' - 6 3/16"; F-((D-A)/2)=7' - 3 31/32"; F-.125"=7' - 6 1/16"; G=4' - 0"; G+((G/5*3)+2")=6' - 4 1/2"; G-(G/5*3)=1' - 8 1/2"; G-2.5"=3' - 8 9/16"; G/10*3=1' - 1 3/4"; G/5*3=2' - 3 1/2"; H=8' - 1"; INLET=4' - 7"; INLET/2=2' - 3 1/2"; J=3' - 4 3/4"; K=0' - 3"; L=3' - 2 1/16"; M=6' - 4 1/8"; M/2=3' - 2 1/16"; N=1' - 0"; P=7' - 6 5/8"; P-N=-6' - 6 5/8"; P-N-M=0' - 2 1/2"; R=0' - 3 7/16"; R+R=0' - 6 7/8"; R/2=0' - 1 23/32"; S=6' - 1 5/8"; T=3' - 0 13/16"; Type Comments=Airfoil Centrifugal Blower Counter-Clockwise Down Blast Arrangement 3 Class 3; U=2' - 2 1/2"; V=1' - 6"; W=0' - 1 1/16"; W/2=0' - 0 17/32"; X=6' - 5 1/2"; X/2=3' - 2 3/4"
- 540_CA-DWDI_CCW_DBD_CLASS_2: ((B+.25")/2)=3' - 3 3/32"; (D-A-.25)/2=0' - 2 3/32"; (G/5*3)+2"=2' - 7"; (M-(B+.25"))/2=0' - 2 7/8"; -((B+.25")/2)=-3' - 3 3/32"; -B/2=-3' - 2 31/32"; -P=-8' - 3 15/16"; A=4' - 7 3/4"; A+.25"=4' - 8"; A+.25"+DB_H=4' - 11"; A/2=2' - 3 7/8"; B=6' - 5 15/16"; B+.25"=6' - 6 3/16"; B/2=3' - 2 31/32"; D=5' - 0 3/16"; D/2=2' - 6 3/32"; DB_D=8' - 8 1/4"; DB_E=4' - 5"; DB_F=8' - 10 5/8"; DB_G=5' - 1 3/4"; DB_H=0' - 3"; E=6' - 10 3/8"; E/2=3' - 5 3/16"; F=8' - 3 1/2"; F-((D-A)/2)=8' - 1 9/32"; F-.125"=8' - 3 3/8"; G=4' - 5"; G+((G/5*3)+2")=7' - 0"; G-(G/5*3)=1' - 11"; G-2.5"=4' - 1 1/16"; G/10*3=1' - 3"; G/5*3=2' - 6"; H=8' - 10 5/8"; INLET=5' - 0"; INLET/2=2' - 6"; J=3' - 8 7/8"; K=0' - 3"; L=3' - 5 31/32"; M=6' - 11 15/16"; M/2=3' - 5 31/32"; N=1' - 1 3/4"; P=8' - 3 15/16"; P-N=-7' - 2 3/16"; P-N-M=0' - 2 1/4"; R=0' - 3 15/16"; R+R=0' - 7 7/8"; R/2=0' - 1 31/32"; S=6' - 9 7/16"; T=3' - 4 23/32"; Type Comments=Airfoil Centrifugal Blower Counter-Clockwise Down Blast Arrangement 3 Class 2; U=2' - 5"; V=1' - 8"; W=0' - 1 1/16"; W/2=0' - 0 17/32"; X=7' - 4 5/16"; X/2=3' - 8 5/32"
- 540_CA-DWDI_CCW_DBD_CLASS_3: ((B+.25")/2)=3' - 3 3/32"; (D-A-.25)/2=0' - 2 3/32"; (G/5*3)+2"=2' - 7"; (M-(B+.25"))/2=0' - 2 7/8"; -((B+.25")/2)=-3' - 3 3/32"; -B/2=-3' - 2 31/32"; -P=-8' - 4 3/16"; A=4' - 7 3/4"; A+.25"=4' - 8"; A+.25"+DB_H=4' - 11"; A/2=2' - 3 7/8"; B=6' - 5 15/16"; B+.25"=6' - 6 3/16"; B/2=3' - 2 31/32"; D=5' - 0 3/16"; D/2=2' - 6 3/32"; DB_D=8' - 8 1/4"; DB_E=4' - 5"; DB_F=8' - 10 5/8"; DB_G=5' - 1 3/4"; DB_H=0' - 3"; E=6' - 10 3/8"; E/2=3' - 5 3/16"; F=8' - 3 1/2"; F-((D-A)/2)=8' - 1 9/32"; F-.125"=8' - 3 3/8"; G=4' - 5"; G+((G/5*3)+2")=7' - 0"; G-(G/5*3)=1' - 11"; G-2.5"=4' - 1 1/16"; G/10*3=1' - 3"; G/5*3=2' - 6"; H=8' - 10 5/8"; INLET=5' - 0"; INLET/2=2' - 6"; J=3' - 8 7/8"; K=0' - 3"; L=3' - 5 31/32"; M=6' - 11 15/16"; M/2=3' - 5 31/32"; N=1' - 2 3/16"; P=8' - 4 3/16"; P-N=-7' - 2"; P-N-M=0' - 2 1/16"; R=0' - 3 15/16"; R+R=0' - 7 7/8"; R/2=0' - 1 31/32"; S=6' - 9 7/16"; T=3' - 4 23/32"; Type Comments=Airfoil Centrifugal Blower Counter-Clockwise Down Blast Arrangement 3 Class 3; U=2' - 5"; V=1' - 8"; W=0' - 1 1/16"; W/2=0' - 0 17/32"; X=7' - 4 5/16"; X/2=3' - 8 5/32"
- 600_CA-DWDI_CCW_DBD_CLASS_2: ((B+.25")/2)=3' - 7 1/4"; (D-A-.25)/2=0' - 2 3/32"; (G/5*3)+2"=2' - 10"; (M-(B+.25"))/2=0' - 2 7/8"; -((B+.25")/2)=-3' - 7 1/4"; -B/2=-3' - 7 1/8"; -P=-9' - 0 3/4"; A=5' - 2 3/16"; A+.25"=5' - 2 7/16"; A+.25"+DB_H=5' - 5 7/16"; A/2=2' - 7 3/32"; B=7' - 2 1/4"; B+.25"=7' - 2 1/2"; B/2=3' - 7 1/8"; D=5' - 6 5/8"; D/2=2' - 9 5/16"; DB_D=9' - 8"; DB_E=4' - 11"; DB_F=9' - 10"; DB_G=5' - 8 1/4"; DB_H=0' - 3"; E=7' - 6 11/16"; E/2=3' - 9 11/32"; F=9' - 2 11/16"; F-((D-A)/2)=9' - 0 15/32"; F-.125"=9' - 2 9/16"; G=4' - 11"; G+((G/5*3)+2")=7' - 9"; G-(G/5*3)=2' - 2"; G-2.5"=4' - 7 1/16"; G/10*3=1' - 4 1/2"; G/5*3=2' - 9"; H=9' - 10"; INLET=5' - 6"; INLET/2=2' - 9"; J=4' - 1 3/4"; K=0' - 3"; L=3' - 10 1/8"; M=7' - 8 1/4"; M/2=3' - 10 1/8"; N=1' - 2 1/4"; P=9' - 0 3/4"; P-N=-7' - 10 1/2"; P-N-M=0' - 2 1/4"; R=0' - 3 15/16"; R+R=0' - 7 7/8"; R/2=0' - 1 31/32"; S=7' - 5 3/4"; T=3' - 8 7/8"; Type Comments=Airfoil Centrifugal Blower Counter-Clockwise Down Blast Arrangement 3 Class 2; U=2' - 8"; V=1' - 10"; W=0' - 1 1/16"; W/2=0' - 0 17/32"; X=8' - 0 5/8"; X/2=4' - 0 5/16"
- 600_CA-DWDI_CCW_DBD_CLASS_3: ((B+.25")/2)=3' - 7 1/4"; (D-A-.25)/2=0' - 2 3/32"; (G/5*3)+2"=2' - 10"; (M-(B+.25"))/2=0' - 2 7/8"; -((B+.25")/2)=-3' - 7 1/4"; -B/2=-3' - 7 1/8"; -P=-9' - 2 3/4"; A=5' - 2 3/16"; A+.25"=5' - 2 7/16"; A+.25"+DB_H=5' - 5 7/16"; A/2=2' - 7 3/32"; B=7' - 2 1/4"; B+.25"=7' - 2 1/2"; B/2=3' - 7 1/8"; D=5' - 6 5/8"; D/2=2' - 9 5/16"; DB_D=9' - 8"; DB_E=4' - 11"; DB_F=9' - 10"; DB_G=5' - 8 1/4"; DB_H=0' - 3"; E=7' - 6 11/16"; E/2=3' - 9 11/32"; F=9' - 2 11/16"; F-((D-A)/2)=9' - 0 15/32"; F-.125"=9' - 2 9/16"; G=4' - 11"; G+((G/5*3)+2")=7' - 9"; G-(G/5*3)=2' - 2"; G-2.5"=4' - 6 9/16"; G/10*3=1' - 4 1/2"; G/5*3=2' - 9"; H=9' - 10"; INLET=5' - 6"; INLET/2=2' - 9"; J=4' - 1 3/4"; K=0' - 3"; L=3' - 10 1/8"; M=7' - 8 1/4"; M/2=3' - 10 1/8"; N=1' - 2 3/4"; P=9' - 2 3/4"; P-N=-8' - 0"; P-N-M=0' - 3 3/4"; R=0' - 4 7/16"; R+R=0' - 8 7/8"; R/2=0' - 2 7/32"; S=7' - 5 3/4"; T=3' - 8 7/8"; Type Comments=Airfoil Centrifugal Blower Counter-Clockwise Down Blast Arrangement 3 Class 3; U=2' - 8"; V=1' - 10"; W=0' - 1 1/16"; W/2=0' - 0 17/32"; X=8' - 0 5/8"; X/2=4' - 0 5/16"
- 660_CA-DWDI_CCW_DBD_CLASS_2: ((B+.25")/2)=3' - 11 9/16"; (D-A-.25)/2=0' - 2 3/32"; (G/5*3)+2"=3' - 1"; (M-(B+.25"))/2=0' - 2 7/8"; -((B+.25")/2)=-3' - 11 9/16"; -B/2=-3' - 11 7/16"; -P=-9' - 10 5/8"; A=5' - 8 7/16"; A+.25"=5' - 8 11/16"; A+.25"+DB_H=5' - 11 11/16"; A/2=2' - 10 7/32"; B=7' - 10 7/8"; B+.25"=7' - 11 1/8"; B/2=3' - 11 7/16"; D=6' - 0 7/8"; D/2=3' - 0 7/16"; DB_D=10' - 1 5/8"; DB_E=5' - 5"; DB_F=10' - 9 3/8"; DB_G=6' - 2 3/4"; DB_H=0' - 3"; E=8' - 3 5/16"; E/2=4' - 1 21/32"; F=10' - 1 7/8"; F-((D-A)/2)=9' - 11 21/32"; F-.125"=10' - 1 3/4"; G=5' - 5"; G+((G/5*3)+2")=8' - 6"; G-(G/5*3)=2' - 5"; G-2.5"=5' - 0 9/16"; G/10*3=1' - 6"; G/5*3=3' - 0"; H=10' - 9 3/8"; INLET=6' - 0"; INLET/2=3' - 0"; J=4' - 6 5/8"; K=0' - 3"; L=4' - 2 7/16"; M=8' - 4 7/8"; M/2=4' - 2 7/16"; N=1' - 3 5/16"; P=9' - 10 5/8"; P-N=-8' - 7 5/16"; P-N-M=0' - 2 7/16"; R=0' - 4 7/16"; R+R=0' - 8 7/8"; R/2=0' - 2 7/32"; S=8' - 2 3/8"; T=4' - 1 3/16"; Type Comments=Airfoil Centrifugal Blower Counter-Clockwise Down Blast Arrangement 3 Class 2; U=2' - 11"; V=2' - 1"; W=0' - 1 1/16"; W/2=0' - 0 17/32"; X=8' - 9 1/4"; X/2=4' - 4 5/8"
- 660_CA-DWDI_CCW_DBD_CLASS_3: ((B+.25")/2)=3' - 11 9/16"; (D-A-.25)/2=0' - 2 3/32"; (G/5*3)+2"=3' - 1"; (M-(B+.25"))/2=0' - 2 7/8"; -((B+.25")/2)=-3' - 11 9/16"; -B/2=-3' - 11 7/16"; -P=-9' - 11 7/8"; A=5' - 8 7/16"; A+.25"=5' - 8 11/16"; A+.25"+DB_H=5' - 11 11/16"; A/2=2' - 10 7/32"; B=7' - 10 7/8"; B+.25"=7' - 11 1/8"; B/2=3' - 11 7/16"; D=6' - 0 7/8"; D/2=3' - 0 7/16"; DB_D=10' - 1 5/8"; DB_E=5' - 5"; DB_F=10' - 9 3/8"; DB_G=6' - 2 3/4"; DB_H=0' - 3"; E=8' - 3 5/16"; E/2=4' - 1 21/32"; F=10' - 1 7/8"; F-((D-A)/2)=9' - 11 21/32"; F-.125"=10' - 1 3/4"; G=5' - 5"; G+((G/5*3)+2")=8' - 6"; G-(G/5*3)=2' - 5"; G-2.5"=5' - 0 9/16"; G/10*3=1' - 6"; G/5*3=3' - 0"; H=10' - 9 3/8"; INLET=6' - 0"; INLET/2=3' - 0"; J=4' - 6 5/8"; K=0' - 3"; L=4' - 2 7/16"; M=8' - 4 7/8"; M/2=4' - 2 7/16"; N=1' - 2 5/8"; P=9' - 11 7/8"; P-N=-8' - 9 1/4"; P-N-M=0' - 4 3/8"; R=0' - 4 7/16"; R+R=0' - 8 7/8"; R/2=0' - 2 7/32"; S=8' - 2 3/8"; T=4' - 1 3/16"; Type Comments=Airfoil Centrifugal Blower Counter-Clockwise Down Blast Arrangement 3 Class 3; U=2' - 11"; V=2' - 1"; W=0' - 1 1/16"; W/2=0' - 0 17/32"; X=8' - 9 1/4"; X/2=4' - 4 5/8"
- 730 _CA-DWDI_CCW_DBD_CLASS_2: ((B+.25")/2)=4' - 4 1/2"; (D-A-.25)/2=0' - 2 3/32"; (G/5*3)+2"=3' - 4 1/2"; (M-(B+.25"))/2=0' - 2 7/8"; -((B+.25")/2)=-4' - 4 1/2"; -B/2=-4' - 4 3/8"; -P=-10' - 10 3/4"; A=6' - 3 13/16"; A+.25"=6' - 4 1/16"; A+.25"+DB_H=6' - 7 1/16"; A/2=3' - 1 29/32"; B=8' - 8 3/4"; B+.25"=8' - 9"; B/2=4' - 4 3/8"; D=6' - 8 1/4"; D/2=3' - 4 1/8"; DB_D=11' - 9 5/16"; DB_E=6' - 0"; DB_F=11' - 10 5/8"; DB_G=6' - 10 3/8"; DB_H=0' - 3"; E=9' - 1 3/16"; E/2=4' - 6 19/32"; F=11' - 2 7/8"; F-((D-A)/2)=11' - 0 21/32"; F-.125"=11' - 2 3/4"; G=6' - 0"; G+((G/5*3)+2")=9' - 4 1/2"; G-(G/5*3)=2' - 8 1/2"; G-2.5"=5' - 7 9/16"; G/10*3=1' - 7 3/4"; G/5*3=3' - 3 1/2"; H=11' - 10 5/8"; INLET=6' - 7"; INLET/2=3' - 3 1/2"; J=5' - 0 1/4"; K=0' - 3"; L=4' - 7 3/8"; M=9' - 2 3/4"; M/2=4' - 7 3/8"; N=1' - 4 1/4"; P=10' - 10 3/4"; P-N=-9' - 6 1/2"; P-N-M=0' - 3 3/4"; R=0' - 4 7/16"; R+R=0' - 8 7/8"; R/2=0' - 2 7/32"; S=9' - 0 1/4"; T=4' - 6 1/8"; Type Comments=Airfoil Centrifugal Blower Counter-Clockwise Down Blast Arrangement 3 Class 2; U=3' - 2 1/2"; V=2' - 4"; W=0' - 1 1/16"; W/2=0' - 0 17/32"; X=9' - 7 1/8"; X/2=4' - 9 9/16"
- 730 _CA-DWDI_CCW_DBD_CLASS_3: ((B+.25")/2)=4' - 4 1/2"; (D-A-.25)/2=0' - 2 3/32"; (G/5*3)+2"=3' - 4 1/2"; (M-(B+.25"))/2=0' - 2 7/8"; -((B+.25")/2)=-4' - 4 1/2"; -B/2=-4' - 4 3/8"; -P=-10' - 11 1/4"; A=6' - 3 13/16"; A+.25"=6' - 4 1/16"; A+.25"+DB_H=6' - 7 1/16"; A/2=3' - 1 29/32"; B=8' - 8 3/4"; B+.25"=8' - 9"; B/2=4' - 4 3/8"; D=6' - 8 1/4"; D/2=3' - 4 1/8"; DB_D=11' - 9 5/16"; DB_E=6' - 0"; DB_F=11' - 10 5/8"; DB_G=6' - 10 3/8"; DB_H=0' - 3"; E=9' - 1 3/16"; E/2=4' - 6 19/32"; F=11' - 2 7/8"; F-((D-A)/2)=11' - 0 21/32"; F-.125"=11' - 2 3/4"; G=6' - 0"; G+((G/5*3)+2")=9' - 4 1/2"; G-(G/5*3)=2' - 8 1/2"; G-2.5"=5' - 7 1/16"; G/10*3=1' - 7 3/4"; G/5*3=3' - 3 1/2"; H=11' - 10 5/8"; INLET=6' - 7"; INLET/2=3' - 3 1/2"; J=5' - 0 1/4"; K=0' - 3"; L=4' - 7 3/8"; M=9' - 2 3/4"; M/2=4' - 7 3/8"; N=1' - 4 3/4"; P=10' - 11 1/4"; P-N=-9' - 6 1/2"; P-N-M=0' - 3 3/4"; R=0' - 4 15/16"; R+R=0' - 9 7/8"; R/2=0' - 2 15/32"; S=9' - 0 1/4"; T=4' - 6 1/8"; Type Comments=Airfoil Centrifugal Blower Counter-Clockwise Down Blast Arrangement 3 Class 3; U=3' - 2 1/2"; V=2' - 4"; W=0' - 1 1/16"; W/2=0' - 0 17/32"; X=9' - 7 1/8"; X/2=4' - 9 9/16"

## geometry (parser evidence)
native form markers: Sweep x3
no freeform markers — native parametric forms only
